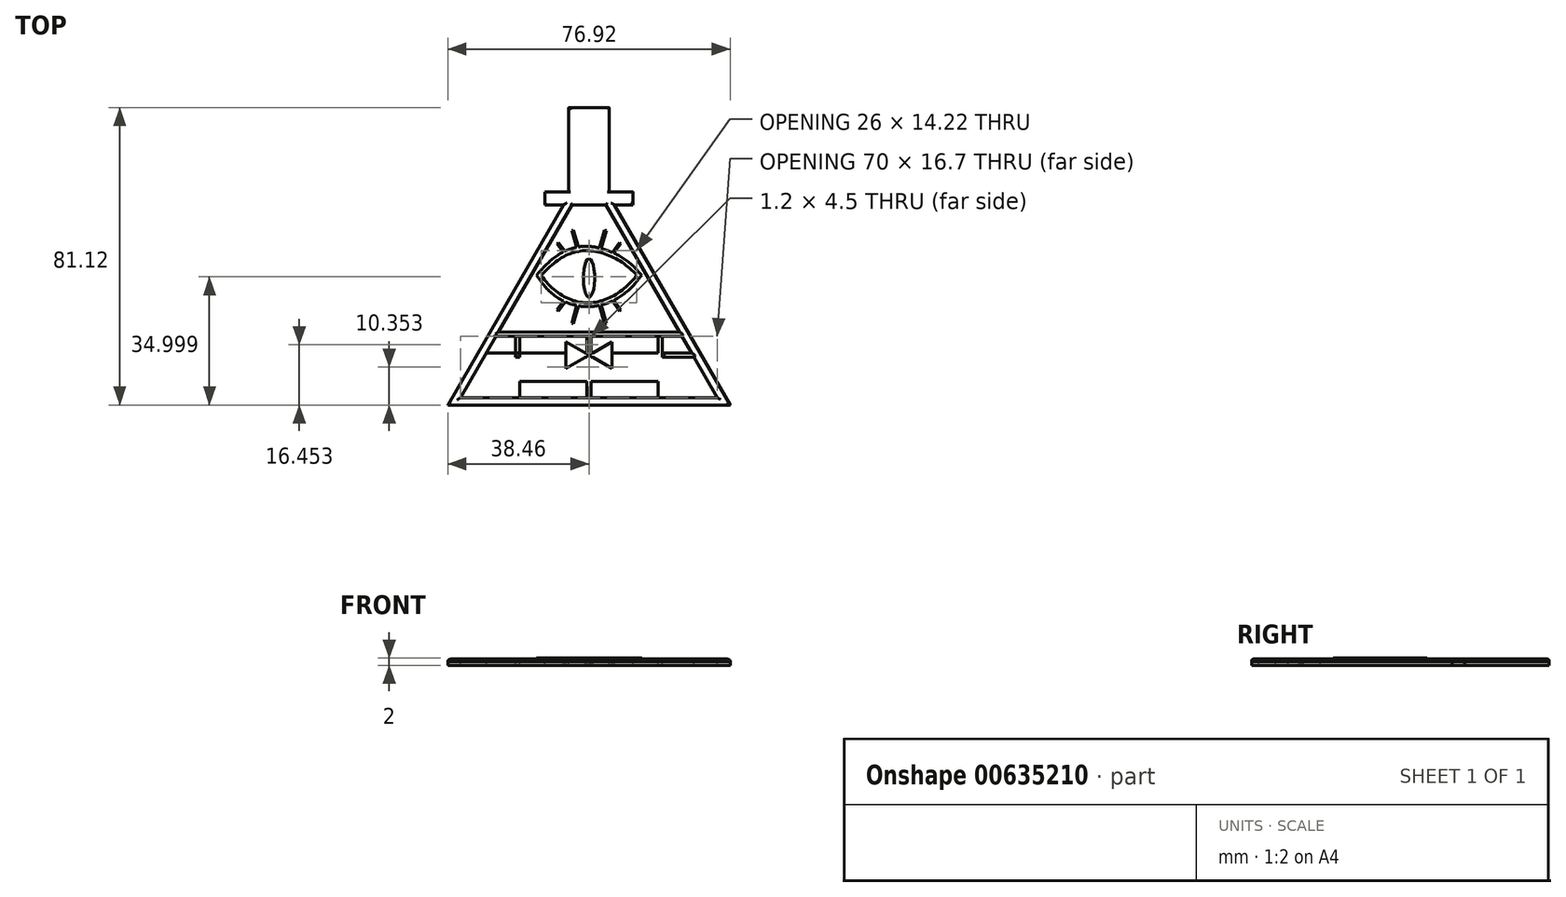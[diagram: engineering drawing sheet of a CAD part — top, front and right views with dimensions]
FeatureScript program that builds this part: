
annotation { "Feature Type Name" : "Feature", "Feature Type Description" : "" }
export const myFeature = defineFeature(function(context is Context, id is Id, definition is map)
    precondition{}
    {
        {
            var Q0;
            Q0=qCreatedBy(makeId("Top.planeOp"),FACE);
            var sketch = newSketch(context, id + "F0", { "sketchPlane" : qUnion([Q0])});
            skCircle(sketch, "E0.cCircle", {"center": v(0, 0) * mm, "radius": 20.2 * mm, "construction": true});
            skLineSegment(sketch, "E0.0", {"start": v(35, -20.2) * mm, "end": v(-35, -20.2) * mm});
            skLineSegment(sketch, "E0.1", {"start": v(-35, -20.2) * mm, "end": v(0, 40.41) * mm});
            skLineSegment(sketch, "E0.2", {"start": v(0, 40.41) * mm, "end": v(35, -20.2) * mm});
            skPoint(sketch, "E0.0.midPoint", {"position": v(0, -20.2) * mm});
            skLineSegment(sketch, "E1", {"start": v(0, 32.41) * mm, "end": v(12, 32.41) * mm});
            skLineSegment(sketch, "E2", {"start": v(12, 32.41) * mm, "end": v(12, 35.91) * mm});
            skLineSegment(sketch, "E3", {"start": v(12, 35.91) * mm, "end": v(-12, 35.91) * mm});
            skLineSegment(sketch, "E4", {"start": v(-12, 35.91) * mm, "end": v(-12, 32.41) * mm});
            skLineSegment(sketch, "E5", {"start": v(-12, 32.41) * mm, "end": v(0, 32.41) * mm});
            skLineSegment(sketch, "E6", {"start": v(0, 40.41) * mm, "end": v(0, 35.91) * mm});
            skLineSegment(sketch, "E7", {"start": v(-12, 35.91) * mm, "end": v(-5.5, 35.91) * mm});
            skLineSegment(sketch, "E8", {"start": v(-5.5, 35.91) * mm, "end": v(-5.5, 58.91) * mm});
            skLineSegment(sketch, "E9", {"start": v(12, 35.91) * mm, "end": v(6, 35.91) * mm});
            skPoint(sketch, "E9.endSnap0", {"position": v(6, 32.41) * mm});
            skLineSegment(sketch, "E10", {"start": v(12, 35.91) * mm, "end": v(5.5, 35.91) * mm});
            skLineSegment(sketch, "E11", {"start": v(5.5, 35.91) * mm, "end": v(5.5, 58.91) * mm});
            skLineSegment(sketch, "E12", {"start": v(5.5, 58.91) * mm, "end": v(-5.5, 58.91) * mm});
            skPoint(sketch, "E13", {"position": v(0, 12.4) * mm});
            skLineSegment(sketch, "E14", {"start": v(0, 5.68) * mm, "end": v(0, 19.9) * mm});
            skLineSegment(sketch, "E15", {"start": v(-13, 13.17) * mm, "end": v(13, 13.17) * mm});
            skFitSpline(sketch, "E16", {"points": [v(-13, 13.17) * mm, v(0, 19.9) * mm, v(13, 13.17) * mm], "startDerivative": vector(26.44, 29.26) * mm, "endDerivative": vector(19.77, -23.2) * mm});
            skFitSpline(sketch, "E17", {"points": [v(-13, 13.17) * mm, v(0, 5.68) * mm, v(13, 13.17) * mm], "startDerivative": vector(20.09, -29.42) * mm, "endDerivative": vector(20.07, 26.4) * mm});
            skLineSegment(sketch, "E18.0", {"start": v(38.46, -22.2) * mm, "end": v(-38.46, -22.2) * mm});
            skLineSegment(sketch, "E18.1", {"start": v(0, 44.41) * mm, "end": v(38.46, -22.2) * mm});
            skLineSegment(sketch, "E18.2", {"start": v(-38.46, -22.2) * mm, "end": v(0, 44.41) * mm});
            skEllipse(sketch, "E19", {"center": v(0, 12.4) * mm, "majorRadius": 5.25 * mm, "minorRadius": 1.53 * mm, "majorAxis": v(0, 1)});
            skFitSpline(sketch, "E20.0", {"points": [v(-13.74, 13.84) * mm, v(-12.61, 15.1) * mm, v(-10.4, 17.25) * mm, v(-7.04, 19.51) * mm, v(-3.58, 20.78) * mm, v(0.03, 21.05) * mm, v(3.79, 20.38) * mm, v(7.48, 18.9) * mm, v(10.92, 16.7) * mm, v(12.9, 14.84) * mm, v(13.76, 13.82) * mm]});
            skFitSpline(sketch, "E21.0", {"points": [v(-13.83, 12.6) * mm, v(-12.95, 11.33) * mm, v(-11, 9.04) * mm, v(-7.6, 6.5) * mm, v(-4.5, 5.22) * mm, v(-1.93, 4.73) * mm, v(0.03, 4.63) * mm, v(1.98, 4.83) * mm, v(4.54, 5.44) * mm, v(7.62, 6.82) * mm, v(10.98, 9.3) * mm, v(12.92, 11.42) * mm, v(13.8, 12.57) * mm]});
            skLineSegment(sketch, "E22", {"start": v(-11.84, 10.11) * mm, "end": v(-14.33, 13.23) * mm});
            skLineSegment(sketch, "E23", {"start": v(-13.6, 14) * mm, "end": v(-14.33, 13.23) * mm});
            skLineSegment(sketch, "E24.MirrorCS", {"start": v(13.6, 14) * mm, "end": v(14.33, 13.23) * mm});
            skLineSegment(sketch, "E25", {"start": v(13.11, 11.7) * mm, "end": v(14.33, 13.23) * mm});
            skLineSegment(sketch, "E26", {"start": v(-6.93, 19.4) * mm, "end": v(-8.7, 21.82) * mm});
            skLineSegment(sketch, "E27", {"start": v(-8.7, 21.82) * mm, "end": v(-8.29, 22.12) * mm});
            skLineSegment(sketch, "E28", {"start": v(-8.29, 22.12) * mm, "end": v(-6.48, 19.62) * mm});
            skLineSegment(sketch, "E29.MirrorCS", {"start": v(8.29, 22.12) * mm, "end": v(6.48, 19.62) * mm});
            skLineSegment(sketch, "E30.MirrorCS", {"start": v(6.93, 19.4) * mm, "end": v(8.7, 21.82) * mm});
            skLineSegment(sketch, "E31.MirrorCS", {"start": v(8.7, 21.82) * mm, "end": v(8.29, 22.12) * mm});
            skLineSegment(sketch, "E32", {"start": v(6.48, 19.62) * mm, "end": v(6.28, 19.33) * mm});
            skLineSegment(sketch, "E33", {"start": v(6.93, 19.4) * mm, "end": v(6.74, 19.12) * mm});
            skLineSegment(sketch, "E34", {"start": v(-2.88, 20.75) * mm, "end": v(-4.23, 25.56) * mm});
            skLineSegment(sketch, "E35", {"start": v(-4.23, 25.56) * mm, "end": v(-4.7, 25.43) * mm});
            skLineSegment(sketch, "E36", {"start": v(-4.7, 25.43) * mm, "end": v(-3.38, 20.65) * mm});
            skLineSegment(sketch, "E37.MirrorCS", {"start": v(2.88, 20.75) * mm, "end": v(4.23, 25.56) * mm});
            skLineSegment(sketch, "E38.MirrorCS", {"start": v(4.7, 25.43) * mm, "end": v(3.38, 20.65) * mm});
            skLineSegment(sketch, "E39.MirrorCS", {"start": v(4.23, 25.56) * mm, "end": v(4.7, 25.43) * mm});
            skLineSegment(sketch, "E40", {"start": v(3.38, 20.65) * mm, "end": v(3.3, 20.38) * mm});
            skLineSegment(sketch, "E41", {"start": v(2.88, 20.75) * mm, "end": v(2.81, 20.5) * mm});
            skLineSegment(sketch, "E42", {"start": v(0, 12.79) * mm, "end": v(-0.93, 12.79) * mm});
            skLineSegment(sketch, "E43.MirrorCS", {"start": v(-2.88, 4.83) * mm, "end": v(-4.23, 0.02) * mm});
            skLineSegment(sketch, "E44.MirrorCS", {"start": v(-4.7, 0.15) * mm, "end": v(-3.38, 4.92) * mm});
            skLineSegment(sketch, "E45.MirrorCS", {"start": v(-8.29, 3.46) * mm, "end": v(-6.48, 5.96) * mm});
            skLineSegment(sketch, "E46.MirrorCS", {"start": v(-6.93, 6.19) * mm, "end": v(-8.7, 3.76) * mm});
            skLineSegment(sketch, "E47.MirrorCS", {"start": v(-4.23, 0.02) * mm, "end": v(-4.7, 0.15) * mm});
            skLineSegment(sketch, "E48.MirrorCS", {"start": v(-8.7, 3.76) * mm, "end": v(-8.29, 3.46) * mm});
            skLineSegment(sketch, "E49.MirrorCS", {"start": v(4.23, 0.02) * mm, "end": v(4.7, 0.15) * mm});
            skLineSegment(sketch, "E50.MirrorCS", {"start": v(2.88, 4.83) * mm, "end": v(4.23, 0.02) * mm});
            skLineSegment(sketch, "E51.MirrorCS", {"start": v(4.7, 0.15) * mm, "end": v(3.38, 4.92) * mm});
            skLineSegment(sketch, "E52.MirrorCS", {"start": v(8.7, 3.76) * mm, "end": v(8.29, 3.46) * mm});
            skLineSegment(sketch, "E53.MirrorCS", {"start": v(8.29, 3.46) * mm, "end": v(6.48, 5.96) * mm});
            skLineSegment(sketch, "E54.MirrorCS", {"start": v(6.93, 6.19) * mm, "end": v(8.7, 3.76) * mm});
            skLineSegment(sketch, "E55", {"start": v(-6.93, 6.19) * mm, "end": v(-6.86, 6.3) * mm});
            skLineSegment(sketch, "E56", {"start": v(-6.48, 5.96) * mm, "end": v(-6.4, 6.07) * mm});
            skLineSegment(sketch, "E57", {"start": v(-3.38, 4.92) * mm, "end": v(-3.35, 5.02) * mm});
            skLineSegment(sketch, "E58", {"start": v(-2.88, 4.83) * mm, "end": v(-2.86, 4.92) * mm});
            skLineSegment(sketch, "E59", {"start": v(2.88, 4.83) * mm, "end": v(2.82, 5.04) * mm});
            skLineSegment(sketch, "E60", {"start": v(3.38, 4.92) * mm, "end": v(3.3, 5.16) * mm});
            skLineSegment(sketch, "E61", {"start": v(6.48, 5.96) * mm, "end": v(6.26, 6.27) * mm});
            skLineSegment(sketch, "E62", {"start": v(6.93, 6.19) * mm, "end": v(6.71, 6.5) * mm});
            skLineSegment(sketch, "E63", {"start": v(-25.36, -3.5) * mm, "end": v(25.36, -3.5) * mm});
            skLineSegment(sketch, "E64", {"start": v(0, -3.5) * mm, "end": v(0, -9.2) * mm, "construction": true});
            skLineSegment(sketch, "E65", {"start": v(0, -9.2) * mm, "end": v(28.65, -9.2) * mm});
            skLineSegment(sketch, "E66", {"start": v(0, -15.7) * mm, "end": v(32.4, -15.7) * mm});
            skLineSegment(sketch, "E67", {"start": v(0, -15.7) * mm, "end": v(0, -20.2) * mm, "construction": true});
            skLineSegment(sketch, "E68", {"start": v(0, -9.2) * mm, "end": v(-28.65, -9.2) * mm});
            skLineSegment(sketch, "E69", {"start": v(0, -15.7) * mm, "end": v(-32.4, -15.7) * mm});
            skLineSegment(sketch, "E70", {"start": v(-19.43, -15.7) * mm, "end": v(-19.43, -20.2) * mm, "construction": true});
            skLineSegment(sketch, "E71", {"start": v(-32.4, -15.7) * mm, "end": v(-19.43, -15.7) * mm});
            skLineSegment(sketch, "E72", {"start": v(-19.43, -15.7) * mm, "end": v(0, -15.7) * mm});
            skLineSegment(sketch, "E73", {"start": v(-9.72, -15.7) * mm, "end": v(-9.72, -9.2) * mm, "construction": true});
            skLineSegment(sketch, "E74", {"start": v(-19.43, -9.2) * mm, "end": v(-19.43, -3.5) * mm, "construction": true});
            skLineSegment(sketch, "E75", {"start": v(32.4, -15.7) * mm, "end": v(19.43, -15.7) * mm});
            skLineSegment(sketch, "E76", {"start": v(19.43, -15.7) * mm, "end": v(19.43, -20.2) * mm, "construction": true});
            skLineSegment(sketch, "E77", {"start": v(19.43, -15.7) * mm, "end": v(0, -15.7) * mm});
            skLineSegment(sketch, "E78", {"start": v(9.72, -15.7) * mm, "end": v(9.72, -9.2) * mm, "construction": true});
            skLineSegment(sketch, "E79", {"start": v(19.43, -9.2) * mm, "end": v(19.43, -3.5) * mm, "construction": true});
            skLineSegment(sketch, "E80", {"start": v(-31.25, -13.7) * mm, "end": v(31.25, -13.7) * mm});
            skLineSegment(sketch, "E81", {"start": v(-27.96, -8) * mm, "end": v(27.96, -8) * mm});
            skLineSegment(sketch, "E82", {"start": v(-24.67, -2.3) * mm, "end": v(24.67, -2.3) * mm});
            skLineSegment(sketch, "E83.bottom", {"start": v(-18.83, -15.7) * mm, "end": v(-20.03, -15.7) * mm});
            skLineSegment(sketch, "E83.top", {"start": v(-18.83, -20.2) * mm, "end": v(-20.03, -20.2) * mm});
            skLineSegment(sketch, "E83.left", {"start": v(-18.83, -15.7) * mm, "end": v(-18.83, -20.2) * mm});
            skLineSegment(sketch, "E83.right", {"start": v(-20.03, -15.7) * mm, "end": v(-20.03, -20.2) * mm});
            skPoint(sketch, "E83.middle", {"position": v(-19.43, -17.96) * mm});
            skLineSegment(sketch, "E84.bottom", {"start": v(0.6, -15.7) * mm, "end": v(-0.6, -15.7) * mm});
            skLineSegment(sketch, "E84.top", {"start": v(0.6, -20.2) * mm, "end": v(-0.6, -20.2) * mm});
            skLineSegment(sketch, "E84.left", {"start": v(0.6, -15.7) * mm, "end": v(0.6, -20.2) * mm});
            skLineSegment(sketch, "E84.right", {"start": v(-0.6, -15.7) * mm, "end": v(-0.6, -20.2) * mm});
            skPoint(sketch, "E84.middle", {"position": v(0, -17.96) * mm});
            skLineSegment(sketch, "E85.bottom", {"start": v(20.03, -15.7) * mm, "end": v(18.83, -15.7) * mm});
            skLineSegment(sketch, "E85.top", {"start": v(20.03, -20.2) * mm, "end": v(18.83, -20.2) * mm});
            skLineSegment(sketch, "E85.left", {"start": v(20.03, -15.7) * mm, "end": v(20.03, -20.2) * mm});
            skLineSegment(sketch, "E85.right", {"start": v(18.83, -15.7) * mm, "end": v(18.83, -20.2) * mm});
            skPoint(sketch, "E85.middle", {"position": v(19.43, -17.96) * mm});
            skLineSegment(sketch, "E86.bottom", {"start": v(-9.12, -15.7) * mm, "end": v(-10.32, -15.7) * mm});
            skLineSegment(sketch, "E86.top", {"start": v(-9.12, -9.2) * mm, "end": v(-10.32, -9.2) * mm});
            skLineSegment(sketch, "E86.left", {"start": v(-9.12, -15.7) * mm, "end": v(-9.12, -9.2) * mm});
            skLineSegment(sketch, "E86.right", {"start": v(-10.32, -15.7) * mm, "end": v(-10.32, -9.2) * mm});
            skPoint(sketch, "E86.middle", {"position": v(-9.72, -12.46) * mm});
            skLineSegment(sketch, "E87.bottom", {"start": v(10.32, -15.7) * mm, "end": v(9.12, -15.7) * mm});
            skLineSegment(sketch, "E87.top", {"start": v(10.32, -9.2) * mm, "end": v(9.12, -9.2) * mm});
            skLineSegment(sketch, "E87.left", {"start": v(10.32, -15.7) * mm, "end": v(10.32, -9.2) * mm});
            skLineSegment(sketch, "E87.right", {"start": v(9.12, -15.7) * mm, "end": v(9.12, -9.2) * mm});
            skPoint(sketch, "E87.middle", {"position": v(9.72, -12.46) * mm});
            skLineSegment(sketch, "E88.bottom", {"start": v(0.6, -9.2) * mm, "end": v(-0.6, -9.2) * mm});
            skLineSegment(sketch, "E88.top", {"start": v(0.6, -3.5) * mm, "end": v(-0.6, -3.5) * mm});
            skLineSegment(sketch, "E88.left", {"start": v(0.6, -9.2) * mm, "end": v(0.6, -3.5) * mm});
            skLineSegment(sketch, "E88.right", {"start": v(-0.6, -9.2) * mm, "end": v(-0.6, -3.5) * mm});
            skPoint(sketch, "E88.middle", {"position": v(0, -6.36) * mm});
            skLineSegment(sketch, "E89.bottom", {"start": v(20.03, -9.2) * mm, "end": v(18.83, -9.2) * mm});
            skLineSegment(sketch, "E89.top", {"start": v(20.03, -3.5) * mm, "end": v(18.83, -3.5) * mm});
            skLineSegment(sketch, "E89.left", {"start": v(20.03, -9.2) * mm, "end": v(20.03, -3.5) * mm});
            skLineSegment(sketch, "E89.right", {"start": v(18.83, -9.2) * mm, "end": v(18.83, -3.5) * mm});
            skPoint(sketch, "E89.middle", {"position": v(19.43, -6.36) * mm});
            skLineSegment(sketch, "E90", {"start": v(-19.43, -9.2) * mm, "end": v(-20.43, -9.2) * mm});
            skLineSegment(sketch, "E91.bottom", {"start": v(-18.83, -9.2) * mm, "end": v(-20.03, -9.2) * mm});
            skLineSegment(sketch, "E91.top", {"start": v(-18.83, -3.5) * mm, "end": v(-20.03, -3.5) * mm});
            skLineSegment(sketch, "E91.left", {"start": v(-18.83, -9.2) * mm, "end": v(-18.83, -3.5) * mm});
            skLineSegment(sketch, "E91.right", {"start": v(-20.03, -9.2) * mm, "end": v(-20.03, -3.5) * mm});
            skPoint(sketch, "E91.middle", {"position": v(-19.43, -6.36) * mm});
            skCircle(sketch, "E92.cCircle", {"center": v(4.2, -8.6) * mm, "radius": 4.2 * mm, "construction": true});
            skLineSegment(sketch, "E92.0", {"start": v(0, -8.6) * mm, "end": v(6.3, -4.97) * mm});
            skLineSegment(sketch, "E92.1", {"start": v(6.3, -4.97) * mm, "end": v(6.3, -12.24) * mm});
            skLineSegment(sketch, "E92.2", {"start": v(6.3, -12.24) * mm, "end": v(0, -8.6) * mm});
            skLineSegment(sketch, "E93.MirrorCS", {"start": v(0, -8.6) * mm, "end": v(-6.3, -4.97) * mm});
            skLineSegment(sketch, "E94.MirrorCS", {"start": v(-6.3, -12.24) * mm, "end": v(0, -8.6) * mm});
            skLineSegment(sketch, "E95.MirrorCS", {"start": v(-6.3, -4.97) * mm, "end": v(-6.3, -12.24) * mm});
            skSolve(sketch);
        }
        {
            var Q0;
            {var subQ1=sQuery(id+"F0.wireOp",EDGE,"E4");Q0=makeQuery(id+"F0.imprint","IMPRINT",FACE,{"disambiguationData":[TD([[makeQuery(id+"F0.imprint","IMPRINT",EDGE,{"derivedFrom":subQ1}),1.0]])]});}
            var Q1;
            {var subQ5=sQuery(id+"F0.wireOp",EDGE,"E2");Q1=makeQuery(id+"F0.imprint","IMPRINT",FACE,{"disambiguationData":[TD([[makeQuery(id+"F0.imprint","IMPRINT",EDGE,{"derivedFrom":subQ5}),1.0]])]});}
            var Q2;
            {var subQ0=sQuery(id+"F0.wireOp",EDGE,"E3");var subQ1=sQuery(id+"F0.wireOp",EDGE,"E0.2");var subQ2=makeQuery(id+"F0.imprint","INTERSECT",VERTEX,{"derivedFrom":[subQ1,subQ0]});Q2=makeQuery(id+"F0.imprint","IMPRINT",FACE,{"disambiguationData":[TD([[makeQuery(id+"F0.imprint","IMPRINT",EDGE,{"disambiguationData":[TD([[subQ2,-1.0]])],"derivedFrom":subQ1}),1.0]])]});}
            var Q3;
            {var subQ0=sQuery(id+"F0.wireOp",EDGE,"E5");var subQ1=sQuery(id+"F0.wireOp",EDGE,"E0.1");var subQ2=makeQuery(id+"F0.imprint","INTERSECT",VERTEX,{"derivedFrom":[subQ1,subQ0]});Q3=makeQuery(id+"F0.imprint","IMPRINT",FACE,{"disambiguationData":[TD([[makeQuery(id+"F0.imprint","IMPRINT",EDGE,{"disambiguationData":[TD([[subQ2,-1.0]])],"derivedFrom":subQ1}),1.0]])]});}
            var Q4;
            {var subQ4=sQuery(id+"F0.wireOp",EDGE,"E5");var subQ8=sQuery(id+"F0.wireOp",EDGE,"E0.1");var subQ9=makeQuery(id+"F0.imprint","INTERSECT",VERTEX,{"derivedFrom":[subQ8,subQ4]});Q4=makeQuery(id+"F0.imprint","IMPRINT",FACE,{"disambiguationData":[TD([[makeQuery(id+"F0.imprint","IMPRINT",EDGE,{"disambiguationData":[TD([[subQ9,-1.0]])],"derivedFrom":subQ8}),-1.0]])]});}
            var Q5;
            {var subQ0=sQuery(id+"F0.wireOp",EDGE,"E6");Q5=makeQuery(id+"F0.imprint","IMPRINT",FACE,{"disambiguationData":[TD([[makeQuery(id+"F0.imprint","IMPRINT",EDGE,{"derivedFrom":subQ0}),-1.0]])]});}
            var Q6;
            {var subQ0=sQuery(id+"F0.wireOp",EDGE,"E6");Q6=makeQuery(id+"F0.imprint","IMPRINT",FACE,{"disambiguationData":[TD([[makeQuery(id+"F0.imprint","IMPRINT",EDGE,{"derivedFrom":subQ0}),1.0]])]});}
            var Q7;
            {var subQ0=sQuery(id+"F0.wireOp",EDGE,"E3");var subQ5=sQuery(id+"F0.wireOp",EDGE,"E0.2");var subQ7=makeQuery(id+"F0.imprint","INTERSECT",VERTEX,{"derivedFrom":[subQ5,subQ0]});Q7=makeQuery(id+"F0.imprint","IMPRINT",FACE,{"disambiguationData":[TD([[makeQuery(id+"F0.imprint","IMPRINT",EDGE,{"disambiguationData":[TD([[subQ7,1.0]])],"derivedFrom":subQ0}),-1.0]])]});}
            var Q8;
            {var subQ1=sQuery(id+"F0.wireOp",EDGE,"E8");Q8=makeQuery(id+"F0.imprint","IMPRINT",FACE,{"disambiguationData":[TD([[makeQuery(id+"F0.imprint","IMPRINT",EDGE,{"derivedFrom":subQ1}),-1.0]])]});}
            extrude(context, id + "F1", {"entities" : qUnion([Q0, Q1, Q2, Q3, Q4, Q5, Q6, Q7, Q8]), "depth" : 0.7 * mm, "offsetDistance" : 25 * mm});
        }
        {
            var Q0;
            {var subQ1=sQuery(id+"F0.wireOp",EDGE,"E18.0");Q0=makeQuery(id+"F0.imprint","IMPRINT",FACE,{"disambiguationData":[TD([[makeQuery(id+"F0.imprint","IMPRINT",EDGE,{"derivedFrom":subQ1}),-1.0]])]});}
            var Q1;
            {var subQ5=sQuery(id+"F0.wireOp",EDGE,"E82");Q1=makeQuery(id+"F0.imprint","IMPRINT",FACE,{"disambiguationData":[TD([[makeQuery(id+"F0.imprint","IMPRINT",EDGE,{"derivedFrom":subQ5}),-1.0]])]});}
            var Q2;
            {var subQ5=sQuery(id+"F0.wireOp",EDGE,"E86.top");Q2=makeQuery(id+"F0.imprint","IMPRINT",FACE,{"disambiguationData":[TD([[makeQuery(id+"F0.imprint","IMPRINT",EDGE,{"derivedFrom":subQ5}),-1.0]])]});}
            var Q3;
            {var subQ0=sQuery(id+"F0.wireOp",EDGE,"E90");Q3=makeQuery(id+"F0.imprint","IMPRINT",FACE,{"disambiguationData":[TD([[makeQuery(id+"F0.imprint","IMPRINT",EDGE,{"derivedFrom":subQ0}),-1.0]])]});}
            var Q4;
            {var subQ3=sQuery(id+"F0.wireOp",EDGE,"E81");var subQ6=sQuery(id+"F0.wireOp",EDGE,"E91.right");var subQ7=makeQuery(id+"F0.imprint","INTERSECT",VERTEX,{"derivedFrom":[subQ3,subQ6]});Q4=makeQuery(id+"F0.imprint","IMPRINT",FACE,{"disambiguationData":[TD([[makeQuery(id+"F0.imprint","IMPRINT",EDGE,{"disambiguationData":[TD([[subQ7,-1.0]])],"derivedFrom":subQ3}),-1.0]])]});}
            var Q5;
            {var subQ0=sQuery(id+"F0.wireOp",EDGE,"E87.top");Q5=makeQuery(id+"F0.imprint","IMPRINT",FACE,{"disambiguationData":[TD([[makeQuery(id+"F0.imprint","IMPRINT",EDGE,{"derivedFrom":subQ0}),-1.0]])]});}
            var Q6;
            {var subQ5=sQuery(id+"F0.wireOp",EDGE,"E88.bottom");Q6=makeQuery(id+"F0.imprint","IMPRINT",FACE,{"disambiguationData":[TD([[makeQuery(id+"F0.imprint","IMPRINT",EDGE,{"derivedFrom":subQ5}),-1.0]])]});}
            var Q7;
            {var subQ0=sQuery(id+"F0.wireOp",EDGE,"E65");var subQ1=sQuery(id+"F0.wireOp",EDGE,"E0.2");var subQ2=makeQuery(id+"F0.imprint","INTERSECT",VERTEX,{"derivedFrom":[subQ1,subQ0]});Q7=makeQuery(id+"F0.imprint","IMPRINT",FACE,{"disambiguationData":[TD([[makeQuery(id+"F0.imprint","IMPRINT",EDGE,{"disambiguationData":[TD([[subQ2,1.0]])],"derivedFrom":subQ1}),-1.0]])]});}
            var Q8;
            {var subQ5=sQuery(id+"F0.wireOp",EDGE,"E89.bottom");Q8=makeQuery(id+"F0.imprint","IMPRINT",FACE,{"disambiguationData":[TD([[makeQuery(id+"F0.imprint","IMPRINT",EDGE,{"derivedFrom":subQ5}),-1.0]])]});}
            var Q9;
            {var subQ5=sQuery(id+"F0.wireOp",EDGE,"E89.top");Q9=makeQuery(id+"F0.imprint","IMPRINT",FACE,{"disambiguationData":[TD([[makeQuery(id+"F0.imprint","IMPRINT",EDGE,{"derivedFrom":subQ5}),1.0]])]});}
            var Q10;
            {var subQ5=sQuery(id+"F0.wireOp",EDGE,"E88.top");Q10=makeQuery(id+"F0.imprint","IMPRINT",FACE,{"disambiguationData":[TD([[makeQuery(id+"F0.imprint","IMPRINT",EDGE,{"derivedFrom":subQ5}),1.0]])]});}
            var Q11;
            {var subQ5=sQuery(id+"F0.wireOp",EDGE,"E91.top");Q11=makeQuery(id+"F0.imprint","IMPRINT",FACE,{"disambiguationData":[TD([[makeQuery(id+"F0.imprint","IMPRINT",EDGE,{"derivedFrom":subQ5}),1.0]])]});}
            var Q12;
            {var subQ0=sQuery(id+"F0.wireOp",EDGE,"E71");Q12=makeQuery(id+"F0.imprint","IMPRINT",FACE,{"disambiguationData":[TD([[makeQuery(id+"F0.imprint","IMPRINT",EDGE,{"derivedFrom":subQ0}),1.0]])]});}
            var Q13;
            Q13=makeQuery(id+"F0.imprint","IMPRINT",FACE,{"disambiguationData":[TD([[makeQuery(id+"F0.imprint","IMPRINT",EDGE,{"derivedFrom":sQuery(id+"F0.wireOp",EDGE,"E83.bottom")}),1.0]])]});
            var Q14;
            {var subQ5=sQuery(id+"F0.wireOp",EDGE,"E86.top");Q14=makeQuery(id+"F0.imprint","IMPRINT",FACE,{"disambiguationData":[TD([[makeQuery(id+"F0.imprint","IMPRINT",EDGE,{"derivedFrom":subQ5}),1.0]])]});}
            var Q15;
            {var subQ5=sQuery(id+"F0.wireOp",EDGE,"E86.bottom");Q15=makeQuery(id+"F0.imprint","IMPRINT",FACE,{"disambiguationData":[TD([[makeQuery(id+"F0.imprint","IMPRINT",EDGE,{"derivedFrom":subQ5}),-1.0]])]});}
            var Q16;
            {var subQ0=sQuery(id+"F0.wireOp",EDGE,"E84.bottom");Q16=makeQuery(id+"F0.imprint","IMPRINT",FACE,{"disambiguationData":[TD([[makeQuery(id+"F0.imprint","IMPRINT",EDGE,{"derivedFrom":subQ0}),-1.0]])]});}
            var Q17;
            {var subQ5=sQuery(id+"F0.wireOp",EDGE,"E87.top");Q17=makeQuery(id+"F0.imprint","IMPRINT",FACE,{"disambiguationData":[TD([[makeQuery(id+"F0.imprint","IMPRINT",EDGE,{"derivedFrom":subQ5}),1.0]])]});}
            var Q18;
            {var subQ5=sQuery(id+"F0.wireOp",EDGE,"E87.bottom");Q18=makeQuery(id+"F0.imprint","IMPRINT",FACE,{"disambiguationData":[TD([[makeQuery(id+"F0.imprint","IMPRINT",EDGE,{"derivedFrom":subQ5}),-1.0]])]});}
            var Q19;
            {var subQ8=sQuery(id+"F0.wireOp",EDGE,"E75");Q19=makeQuery(id+"F0.imprint","IMPRINT",FACE,{"disambiguationData":[TD([[makeQuery(id+"F0.imprint","IMPRINT",EDGE,{"derivedFrom":subQ8}),-1.0]])]});}
            var Q20;
            Q20=makeQuery(id+"F0.imprint","IMPRINT",FACE,{"disambiguationData":[TD([[makeQuery(id+"F0.imprint","IMPRINT",EDGE,{"derivedFrom":sQuery(id+"F0.wireOp",EDGE,"E85.bottom")}),1.0]])]});
            var Q21;
            Q21=makeQuery(id+"F0.imprint","IMPRINT",FACE,{"disambiguationData":[TD([[makeQuery(id+"F0.imprint","IMPRINT",EDGE,{"derivedFrom":sQuery(id+"F0.wireOp",EDGE,"E84.bottom")}),1.0]])]});
            var Q22;
            {var subQ1=sQuery(id+"F0.wireOp",EDGE,"E81");var subQ5=sQuery(id+"F0.wireOp",EDGE,"E95.MirrorCS");var subQ6=makeQuery(id+"F0.imprint","INTERSECT",VERTEX,{"derivedFrom":[subQ1,subQ5]});Q22=makeQuery(id+"F0.imprint","IMPRINT",FACE,{"disambiguationData":[TD([[makeQuery(id+"F0.imprint","IMPRINT",EDGE,{"disambiguationData":[TD([[subQ6,-1.0]])],"derivedFrom":subQ1}),-1.0]])]});}
            var Q23;
            {var subQ3=sQuery(id+"F0.wireOp",EDGE,"E95.MirrorCS");var subQ5=sQuery(id+"F0.wireOp",EDGE,"E94.MirrorCS");var subQ6=makeQuery(id+"F0.imprint","INTERSECT",VERTEX,{"derivedFrom":[subQ5,subQ3]});Q23=makeQuery(id+"F0.imprint","IMPRINT",FACE,{"disambiguationData":[TD([[makeQuery(id+"F0.imprint","IMPRINT",EDGE,{"disambiguationData":[TD([[subQ6,-1.0]])],"derivedFrom":subQ5}),1.0]])]});}
            var Q24;
            {var subQ3=sQuery(id+"F0.wireOp",EDGE,"E92.1");var subQ5=sQuery(id+"F0.wireOp",EDGE,"E92.2");var subQ7=makeQuery(id+"F0.imprint","INTERSECT",VERTEX,{"derivedFrom":[subQ3,subQ5]});Q24=makeQuery(id+"F0.imprint","IMPRINT",FACE,{"disambiguationData":[TD([[makeQuery(id+"F0.imprint","IMPRINT",EDGE,{"disambiguationData":[TD([[subQ7,1.0]])],"derivedFrom":subQ3}),-1.0]])]});}
            var Q25;
            {var subQ3=sQuery(id+"F0.wireOp",EDGE,"E92.0");var subQ5=sQuery(id+"F0.wireOp",EDGE,"E81");var subQ6=makeQuery(id+"F0.imprint","INTERSECT",VERTEX,{"derivedFrom":[subQ5,subQ3]});Q25=makeQuery(id+"F0.imprint","IMPRINT",FACE,{"disambiguationData":[TD([[makeQuery(id+"F0.imprint","IMPRINT",EDGE,{"disambiguationData":[TD([[subQ6,-1.0]])],"derivedFrom":subQ5}),-1.0]])]});}
            var Q26;
            {var subQ0=sQuery(id+"F0.wireOp",EDGE,"E92.0");var subQ1=sQuery(id+"F0.wireOp",EDGE,"E81");var subQ2=makeQuery(id+"F0.imprint","INTERSECT",VERTEX,{"derivedFrom":[subQ1,subQ0]});Q26=makeQuery(id+"F0.imprint","IMPRINT",FACE,{"disambiguationData":[TD([[makeQuery(id+"F0.imprint","IMPRINT",EDGE,{"disambiguationData":[TD([[subQ2,-1.0]])],"derivedFrom":subQ1}),1.0]])]});}
            var Q27;
            {var subQ0=sQuery(id+"F0.wireOp",EDGE,"E95.MirrorCS");var subQ1=sQuery(id+"F0.wireOp",EDGE,"E81");var subQ2=makeQuery(id+"F0.imprint","INTERSECT",VERTEX,{"derivedFrom":[subQ1,subQ0]});Q27=makeQuery(id+"F0.imprint","IMPRINT",FACE,{"disambiguationData":[TD([[makeQuery(id+"F0.imprint","IMPRINT",EDGE,{"disambiguationData":[TD([[subQ2,-1.0]])],"derivedFrom":subQ1}),1.0]])]});}
            var Q28;
            {var subQ0=sQuery(id+"F0.wireOp",EDGE,"E93.MirrorCS");var subQ1=sQuery(id+"F0.wireOp",EDGE,"E81");var subQ2=makeQuery(id+"F0.imprint","INTERSECT",VERTEX,{"derivedFrom":[subQ1,subQ0]});Q28=makeQuery(id+"F0.imprint","IMPRINT",FACE,{"disambiguationData":[TD([[makeQuery(id+"F0.imprint","IMPRINT",EDGE,{"disambiguationData":[TD([[subQ2,-1.0]])],"derivedFrom":subQ1}),-1.0]])]});}
            var Q29;
            {var subQ0=sQuery(id+"F0.wireOp",EDGE,"E88.right");var subQ1=sQuery(id+"F0.wireOp",EDGE,"E81");var subQ2=makeQuery(id+"F0.imprint","INTERSECT",VERTEX,{"derivedFrom":[subQ1,subQ0]});Q29=makeQuery(id+"F0.imprint","IMPRINT",FACE,{"disambiguationData":[TD([[makeQuery(id+"F0.imprint","IMPRINT",EDGE,{"disambiguationData":[TD([[subQ2,-1.0]])],"derivedFrom":subQ1}),-1.0]])]});}
            var Q30;
            {var subQ0=sQuery(id+"F0.wireOp",EDGE,"E88.left");var subQ1=sQuery(id+"F0.wireOp",EDGE,"E81");var subQ2=makeQuery(id+"F0.imprint","INTERSECT",VERTEX,{"derivedFrom":[subQ1,subQ0]});Q30=makeQuery(id+"F0.imprint","IMPRINT",FACE,{"disambiguationData":[TD([[makeQuery(id+"F0.imprint","IMPRINT",EDGE,{"disambiguationData":[TD([[subQ2,-1.0]])],"derivedFrom":subQ1}),-1.0]])]});}
            var Q31;
            {var subQ1=sQuery(id+"F0.wireOp",EDGE,"E88.bottom");var subQ3=sQuery(id+"F0.wireOp",EDGE,"E92.2");var subQ4=makeQuery(id+"F0.imprint","INTERSECT",VERTEX,{"derivedFrom":[subQ1,subQ3]});Q31=makeQuery(id+"F0.imprint","IMPRINT",FACE,{"disambiguationData":[TD([[makeQuery(id+"F0.imprint","IMPRINT",EDGE,{"disambiguationData":[TD([[subQ4,1.0]])],"derivedFrom":subQ1}),-1.0]])]});}
            var Q32;
            {var subQ1=sQuery(id+"F0.wireOp",EDGE,"E88.bottom");var subQ3=sQuery(id+"F0.wireOp",EDGE,"E94.MirrorCS");var subQ4=makeQuery(id+"F0.imprint","INTERSECT",VERTEX,{"derivedFrom":[subQ1,subQ3]});Q32=makeQuery(id+"F0.imprint","IMPRINT",FACE,{"disambiguationData":[TD([[makeQuery(id+"F0.imprint","IMPRINT",EDGE,{"disambiguationData":[TD([[subQ4,-1.0]])],"derivedFrom":subQ1}),-1.0]])]});}
            var Q33;
            {var subQ0=sQuery(id+"F0.wireOp",EDGE,"E94.MirrorCS");var subQ1=sQuery(id+"F0.wireOp",EDGE,"E88.right");var subQ2=makeQuery(id+"F0.imprint","INTERSECT",VERTEX,{"derivedFrom":[subQ1,subQ0]});Q33=makeQuery(id+"F0.imprint","IMPRINT",FACE,{"disambiguationData":[TD([[makeQuery(id+"F0.imprint","IMPRINT",EDGE,{"disambiguationData":[TD([[subQ2,-1.0]])],"derivedFrom":subQ1}),-1.0]])]});}
            var Q34;
            {var subQ0=sQuery(id+"F0.wireOp",EDGE,"E92.2");var subQ1=sQuery(id+"F0.wireOp",EDGE,"E88.left");var subQ2=makeQuery(id+"F0.imprint","INTERSECT",VERTEX,{"derivedFrom":[subQ1,subQ0]});Q34=makeQuery(id+"F0.imprint","IMPRINT",FACE,{"disambiguationData":[TD([[makeQuery(id+"F0.imprint","IMPRINT",EDGE,{"disambiguationData":[TD([[subQ2,-1.0]])],"derivedFrom":subQ1}),1.0]])]});}
            var Q35;
            {var subQ1=sQuery(id+"F0.wireOp",EDGE,"E68");var subQ3=sQuery(id+"F0.wireOp",EDGE,"E94.MirrorCS");var subQ4=makeQuery(id+"F0.imprint","INTERSECT",VERTEX,{"derivedFrom":[subQ1,subQ3]});Q35=makeQuery(id+"F0.imprint","IMPRINT",FACE,{"disambiguationData":[TD([[makeQuery(id+"F0.imprint","IMPRINT",EDGE,{"disambiguationData":[TD([[subQ4,-1.0]])],"derivedFrom":subQ3}),-1.0]])]});}
            var Q36;
            {var subQ1=sQuery(id+"F0.wireOp",EDGE,"E65");var subQ3=sQuery(id+"F0.wireOp",EDGE,"E92.2");var subQ4=makeQuery(id+"F0.imprint","INTERSECT",VERTEX,{"derivedFrom":[subQ1,subQ3]});Q36=makeQuery(id+"F0.imprint","IMPRINT",FACE,{"disambiguationData":[TD([[makeQuery(id+"F0.imprint","IMPRINT",EDGE,{"disambiguationData":[TD([[subQ4,-1.0]])],"derivedFrom":subQ3}),1.0]])]});}
            extrude(context, id + "F2", {"entities" : qUnion([Q0, Q1, Q2, Q3, Q4, Q5, Q6, Q7, Q8, Q9, Q10, Q11, Q12, Q13, Q14, Q15, Q16, Q17, Q18, Q19, Q20, Q21, Q22, Q23, Q24, Q25, Q26, Q27, Q28, Q29, Q30, Q31, Q32, Q33, Q34, Q35, Q36]), "operationType" : NewBodyOperationType.ADD, "depth" : 0.7 * mm, "offsetDistance" : 25 * mm});
        }
        {
            var Q0;
            {var subQ21=sQuery(id+"F0.wireOp",EDGE,"E22");Q0=makeQuery(id+"F0.imprint","IMPRINT",FACE,{"disambiguationData":[TD([[makeQuery(id+"F0.imprint","IMPRINT",EDGE,{"derivedFrom":subQ21}),-1.0]])]});}
            var Q1;
            {var subQ0=sQuery(id+"F0.wireOp",EDGE,"E34");Q1=makeQuery(id+"F0.imprint","IMPRINT",FACE,{"disambiguationData":[TD([[makeQuery(id+"F0.imprint","IMPRINT",EDGE,{"derivedFrom":subQ0}),1.0]])]});}
            var Q2;
            {var subQ0=sQuery(id+"F0.wireOp",EDGE,"E26");Q2=makeQuery(id+"F0.imprint","IMPRINT",FACE,{"disambiguationData":[TD([[makeQuery(id+"F0.imprint","IMPRINT",EDGE,{"derivedFrom":subQ0}),-1.0]])]});}
            var Q3;
            Q3=makeQuery(id+"F0.imprint","IMPRINT",FACE,{"disambiguationData":[TD([[makeQuery(id+"F0.imprint","IMPRINT",EDGE,{"derivedFrom":sQuery(id+"F0.wireOp",EDGE,"E37.MirrorCS")}),-1.0]])]});
            var Q4;
            Q4=makeQuery(id+"F0.imprint","IMPRINT",FACE,{"disambiguationData":[TD([[makeQuery(id+"F0.imprint","IMPRINT",EDGE,{"derivedFrom":sQuery(id+"F0.wireOp",EDGE,"E29.MirrorCS")}),1.0]])]});
            var Q5;
            Q5=makeQuery(id+"F0.imprint","IMPRINT",FACE,{"disambiguationData":[TD([[makeQuery(id+"F0.imprint","IMPRINT",EDGE,{"derivedFrom":sQuery(id+"F0.wireOp",EDGE,"E52.MirrorCS")}),-1.0]])]});
            var Q6;
            Q6=makeQuery(id+"F0.imprint","IMPRINT",FACE,{"disambiguationData":[TD([[makeQuery(id+"F0.imprint","IMPRINT",EDGE,{"derivedFrom":sQuery(id+"F0.wireOp",EDGE,"E49.MirrorCS")}),1.0]])]});
            var Q7;
            Q7=makeQuery(id+"F0.imprint","IMPRINT",FACE,{"disambiguationData":[TD([[makeQuery(id+"F0.imprint","IMPRINT",EDGE,{"derivedFrom":sQuery(id+"F0.wireOp",EDGE,"E43.MirrorCS")}),-1.0]])]});
            var Q8;
            Q8=makeQuery(id+"F0.imprint","IMPRINT",FACE,{"disambiguationData":[TD([[makeQuery(id+"F0.imprint","IMPRINT",EDGE,{"derivedFrom":sQuery(id+"F0.wireOp",EDGE,"E45.MirrorCS")}),1.0]])]});
            var Q9;
            {var subQ0=sQuery(id+"F0.wireOp",EDGE,"E14");var subQ1=makeQuery(id+"F0.imprint","IMPRINT",VERTEX,{"derivedFrom":subQ0});Q9=makeQuery(id+"F0.imprint","IMPRINT",FACE,{"disambiguationData":[TD([[makeQuery(id+"F0.imprint","IMPRINT",EDGE,{"disambiguationData":[TD([[subQ1,1.0]])],"derivedFrom":subQ0}),-1.0]])]});}
            var Q10;
            {var subQ0=sQuery(id+"F0.wireOp",EDGE,"E14");var subQ1=makeQuery(id+"F0.imprint","IMPRINT",VERTEX,{"derivedFrom":subQ0});Q10=makeQuery(id+"F0.imprint","IMPRINT",FACE,{"disambiguationData":[TD([[makeQuery(id+"F0.imprint","IMPRINT",EDGE,{"disambiguationData":[TD([[subQ1,1.0]])],"derivedFrom":subQ0}),1.0]])]});}
            var Q11;
            {var subQ0=sQuery(id+"F0.wireOp",EDGE,"E15");var subQ1=sQuery(id+"F0.wireOp",EDGE,"E14");var subQ2=makeQuery(id+"F0.imprint","INTERSECT",VERTEX,{"derivedFrom":[subQ1,subQ0]});Q11=makeQuery(id+"F0.imprint","IMPRINT",FACE,{"disambiguationData":[TD([[makeQuery(id+"F0.imprint","IMPRINT",EDGE,{"disambiguationData":[TD([[subQ2,-1.0]])],"derivedFrom":subQ1}),1.0]])]});}
            var Q12;
            {var subQ0=sQuery(id+"F0.wireOp",EDGE,"E15");var subQ1=sQuery(id+"F0.wireOp",EDGE,"E14");var subQ2=makeQuery(id+"F0.imprint","INTERSECT",VERTEX,{"derivedFrom":[subQ1,subQ0]});Q12=makeQuery(id+"F0.imprint","IMPRINT",FACE,{"disambiguationData":[TD([[makeQuery(id+"F0.imprint","IMPRINT",EDGE,{"disambiguationData":[TD([[subQ2,-1.0]])],"derivedFrom":subQ1}),-1.0]])]});}
            extrude(context, id + "F3", {"entities" : qUnion([Q0, Q1, Q2, Q3, Q4, Q5, Q6, Q7, Q8, Q9, Q10, Q11, Q12]), "depth" : 1 * mm, "offsetDistance" : 25 * mm});
        }
        {
            var Q0;
            {var subQ5=sQuery(id+"F0.wireOp",EDGE,"E82");Q0=makeQuery(id+"F0.imprint","IMPRINT",FACE,{"disambiguationData":[TD([[makeQuery(id+"F0.imprint","IMPRINT",EDGE,{"derivedFrom":subQ5}),-1.0]])]});}
            var Q1;
            {var subQ0=sQuery(id+"F0.wireOp",EDGE,"E6");Q1=makeQuery(id+"F0.imprint","IMPRINT",FACE,{"disambiguationData":[TD([[makeQuery(id+"F0.imprint","IMPRINT",EDGE,{"derivedFrom":subQ0}),-1.0]])]});}
            var Q2;
            {var subQ0=sQuery(id+"F0.wireOp",EDGE,"E84.left");Q2=makeQuery(id+"F0.imprint","IMPRINT",FACE,{"disambiguationData":[TD([[makeQuery(id+"F0.imprint","IMPRINT",EDGE,{"derivedFrom":subQ0}),1.0]])]});}
            var Q3;
            {var subQ0=sQuery(id+"F0.wireOp",EDGE,"E6");Q3=makeQuery(id+"F0.imprint","IMPRINT",FACE,{"disambiguationData":[TD([[makeQuery(id+"F0.imprint","IMPRINT",EDGE,{"derivedFrom":subQ0}),1.0]])]});}
            var Q4;
            {var subQ0=sQuery(id+"F0.wireOp",EDGE,"E86.top");Q4=makeQuery(id+"F0.imprint","IMPRINT",FACE,{"disambiguationData":[TD([[makeQuery(id+"F0.imprint","IMPRINT",EDGE,{"derivedFrom":subQ0}),-1.0]])]});}
            var Q5;
            {var subQ5=sQuery(id+"F0.wireOp",EDGE,"E84.bottom");Q5=makeQuery(id+"F0.imprint","IMPRINT",FACE,{"disambiguationData":[TD([[makeQuery(id+"F0.imprint","IMPRINT",EDGE,{"derivedFrom":subQ5}),-1.0]])]});}
            var Q6;
            {var subQ0=sQuery(id+"F0.wireOp",EDGE,"E90");Q6=makeQuery(id+"F0.imprint","IMPRINT",FACE,{"disambiguationData":[TD([[makeQuery(id+"F0.imprint","IMPRINT",EDGE,{"derivedFrom":subQ0}),-1.0]])]});}
            var Q7;
            {var subQ0=sQuery(id+"F0.wireOp",EDGE,"E16");var subQ1=sQuery(id+"F0.wireOp",EDGE,"E14");var subQ2=makeQuery(id+"F0.imprint","INTERSECT",VERTEX,{"derivedFrom":[subQ1,subQ0]});Q7=makeQuery(id+"F0.imprint","IMPRINT",FACE,{"disambiguationData":[TD([[makeQuery(id+"F0.imprint","IMPRINT",EDGE,{"disambiguationData":[TD([[subQ2,1.0]])],"derivedFrom":subQ1}),-1.0]])]});}
            var Q8;
            {var subQ0=sQuery(id+"F0.wireOp",EDGE,"E17");var subQ1=sQuery(id+"F0.wireOp",EDGE,"E14");var subQ2=makeQuery(id+"F0.imprint","INTERSECT",VERTEX,{"derivedFrom":[subQ1,subQ0]});Q8=makeQuery(id+"F0.imprint","IMPRINT",FACE,{"disambiguationData":[TD([[makeQuery(id+"F0.imprint","IMPRINT",EDGE,{"disambiguationData":[TD([[subQ2,-1.0]])],"derivedFrom":subQ1}),-1.0]])]});}
            var Q9;
            {var subQ4=sQuery(id+"F0.wireOp",EDGE,"E75");Q9=makeQuery(id+"F0.imprint","IMPRINT",FACE,{"disambiguationData":[TD([[makeQuery(id+"F0.imprint","IMPRINT",EDGE,{"derivedFrom":subQ4}),1.0]])]});}
            var Q10;
            {var subQ0=sQuery(id+"F0.wireOp",EDGE,"E92.2");var subQ1=sQuery(id+"F0.wireOp",EDGE,"E65");var subQ2=makeQuery(id+"F0.imprint","INTERSECT",VERTEX,{"derivedFrom":[subQ1,subQ0]});Q10=makeQuery(id+"F0.imprint","IMPRINT",FACE,{"disambiguationData":[TD([[makeQuery(id+"F0.imprint","IMPRINT",EDGE,{"disambiguationData":[TD([[subQ2,-1.0]])],"derivedFrom":subQ1}),-1.0]])]});}
            var Q11;
            {var subQ1=sQuery(id+"F0.wireOp",EDGE,"E8");Q11=makeQuery(id+"F0.imprint","IMPRINT",FACE,{"disambiguationData":[TD([[makeQuery(id+"F0.imprint","IMPRINT",EDGE,{"derivedFrom":subQ1}),-1.0]])]});}
            var Q12;
            {var subQ0=sQuery(id+"F0.wireOp",EDGE,"E17");var subQ1=sQuery(id+"F0.wireOp",EDGE,"E14");var subQ2=makeQuery(id+"F0.imprint","INTERSECT",VERTEX,{"derivedFrom":[subQ1,subQ0]});Q12=makeQuery(id+"F0.imprint","IMPRINT",FACE,{"disambiguationData":[TD([[makeQuery(id+"F0.imprint","IMPRINT",EDGE,{"disambiguationData":[TD([[subQ2,-1.0]])],"derivedFrom":subQ1}),1.0]])]});}
            var Q13;
            {var subQ0=sQuery(id+"F0.wireOp",EDGE,"E94.MirrorCS");var subQ6=sQuery(id+"F0.wireOp",EDGE,"E68");var subQ11=makeQuery(id+"F0.imprint","INTERSECT",VERTEX,{"derivedFrom":[subQ6,subQ0]});Q13=makeQuery(id+"F0.imprint","IMPRINT",FACE,{"disambiguationData":[TD([[makeQuery(id+"F0.imprint","IMPRINT",EDGE,{"disambiguationData":[TD([[subQ11,-1.0]])],"derivedFrom":subQ6}),-1.0]])]});}
            var Q14;
            {var subQ5=sQuery(id+"F0.wireOp",EDGE,"E2");Q14=makeQuery(id+"F0.imprint","IMPRINT",FACE,{"disambiguationData":[TD([[makeQuery(id+"F0.imprint","IMPRINT",EDGE,{"derivedFrom":subQ5}),1.0]])]});}
            var Q15;
            {var subQ0=sQuery(id+"F0.wireOp",EDGE,"E83.left");Q15=makeQuery(id+"F0.imprint","IMPRINT",FACE,{"disambiguationData":[TD([[makeQuery(id+"F0.imprint","IMPRINT",EDGE,{"derivedFrom":subQ0}),1.0]])]});}
            var Q16;
            {var subQ13=sQuery(id+"F0.wireOp",EDGE,"E22");Q16=makeQuery(id+"F0.imprint","IMPRINT",FACE,{"disambiguationData":[TD([[makeQuery(id+"F0.imprint","IMPRINT",EDGE,{"derivedFrom":subQ13}),1.0]])]});}
            var Q17;
            {var subQ3=sQuery(id+"F0.wireOp",EDGE,"E81");var subQ7=sQuery(id+"F0.wireOp",EDGE,"E91.left");var subQ8=makeQuery(id+"F0.imprint","INTERSECT",VERTEX,{"derivedFrom":[subQ3,subQ7]});Q17=makeQuery(id+"F0.imprint","IMPRINT",FACE,{"disambiguationData":[TD([[makeQuery(id+"F0.imprint","IMPRINT",EDGE,{"disambiguationData":[TD([[subQ8,-1.0]])],"derivedFrom":subQ3}),1.0]])]});}
            var Q18;
            {var subQ5=sQuery(id+"F0.wireOp",EDGE,"E92.2");var subQ9=sQuery(id+"F0.wireOp",EDGE,"E65");var subQ10=makeQuery(id+"F0.imprint","INTERSECT",VERTEX,{"derivedFrom":[subQ9,subQ5]});Q18=makeQuery(id+"F0.imprint","IMPRINT",FACE,{"disambiguationData":[TD([[makeQuery(id+"F0.imprint","IMPRINT",EDGE,{"disambiguationData":[TD([[subQ10,-1.0]])],"derivedFrom":subQ9}),1.0]])]});}
            var Q19;
            {var subQ0=sQuery(id+"F0.wireOp",EDGE,"E14");var subQ1=makeQuery(id+"F0.imprint","IMPRINT",VERTEX,{"derivedFrom":subQ0});Q19=makeQuery(id+"F0.imprint","IMPRINT",FACE,{"disambiguationData":[TD([[makeQuery(id+"F0.imprint","IMPRINT",EDGE,{"disambiguationData":[TD([[subQ1,1.0]])],"derivedFrom":subQ0}),1.0]])]});}
            var Q20;
            {var subQ5=sQuery(id+"F0.wireOp",EDGE,"E87.top");Q20=makeQuery(id+"F0.imprint","IMPRINT",FACE,{"disambiguationData":[TD([[makeQuery(id+"F0.imprint","IMPRINT",EDGE,{"derivedFrom":subQ5}),-1.0]])]});}
            var Q21;
            {var subQ0=sQuery(id+"F0.wireOp",EDGE,"E3");var subQ5=sQuery(id+"F0.wireOp",EDGE,"E0.2");var subQ7=makeQuery(id+"F0.imprint","INTERSECT",VERTEX,{"derivedFrom":[subQ5,subQ0]});Q21=makeQuery(id+"F0.imprint","IMPRINT",FACE,{"disambiguationData":[TD([[makeQuery(id+"F0.imprint","IMPRINT",EDGE,{"disambiguationData":[TD([[subQ7,1.0]])],"derivedFrom":subQ0}),-1.0]])]});}
            var Q22;
            {var subQ0=sQuery(id+"F0.wireOp",EDGE,"E92.0");var subQ1=sQuery(id+"F0.wireOp",EDGE,"E81");var subQ2=makeQuery(id+"F0.imprint","INTERSECT",VERTEX,{"derivedFrom":[subQ1,subQ0]});Q22=makeQuery(id+"F0.imprint","IMPRINT",FACE,{"disambiguationData":[TD([[makeQuery(id+"F0.imprint","IMPRINT",EDGE,{"disambiguationData":[TD([[subQ2,-1.0]])],"derivedFrom":subQ1}),1.0]])]});}
            var Q23;
            {var subQ4=sQuery(id+"F0.wireOp",EDGE,"E71");Q23=makeQuery(id+"F0.imprint","IMPRINT",FACE,{"disambiguationData":[TD([[makeQuery(id+"F0.imprint","IMPRINT",EDGE,{"derivedFrom":subQ4}),-1.0]])]});}
            var Q24;
            {var subQ21=sQuery(id+"F0.wireOp",EDGE,"E22");Q24=makeQuery(id+"F0.imprint","IMPRINT",FACE,{"disambiguationData":[TD([[makeQuery(id+"F0.imprint","IMPRINT",EDGE,{"derivedFrom":subQ21}),-1.0]])]});}
            var Q25;
            {var subQ8=sQuery(id+"F0.wireOp",EDGE,"E75");Q25=makeQuery(id+"F0.imprint","IMPRINT",FACE,{"disambiguationData":[TD([[makeQuery(id+"F0.imprint","IMPRINT",EDGE,{"derivedFrom":subQ8}),-1.0]])]});}
            var Q26;
            {var subQ4=sQuery(id+"F0.wireOp",EDGE,"E5");var subQ8=sQuery(id+"F0.wireOp",EDGE,"E0.1");var subQ9=makeQuery(id+"F0.imprint","INTERSECT",VERTEX,{"derivedFrom":[subQ8,subQ4]});Q26=makeQuery(id+"F0.imprint","IMPRINT",FACE,{"disambiguationData":[TD([[makeQuery(id+"F0.imprint","IMPRINT",EDGE,{"disambiguationData":[TD([[subQ9,-1.0]])],"derivedFrom":subQ8}),-1.0]])]});}
            var Q27;
            {var subQ0=sQuery(id+"F0.wireOp",EDGE,"E16");var subQ1=sQuery(id+"F0.wireOp",EDGE,"E14");var subQ2=makeQuery(id+"F0.imprint","INTERSECT",VERTEX,{"derivedFrom":[subQ1,subQ0]});Q27=makeQuery(id+"F0.imprint","IMPRINT",FACE,{"disambiguationData":[TD([[makeQuery(id+"F0.imprint","IMPRINT",EDGE,{"disambiguationData":[TD([[subQ2,1.0]])],"derivedFrom":subQ1}),1.0]])]});}
            var Q28;
            {var subQ8=sQuery(id+"F0.wireOp",EDGE,"E71");Q28=makeQuery(id+"F0.imprint","IMPRINT",FACE,{"disambiguationData":[TD([[makeQuery(id+"F0.imprint","IMPRINT",EDGE,{"derivedFrom":subQ8}),1.0]])]});}
            var Q29;
            {var subQ0=sQuery(id+"F0.wireOp",EDGE,"E15");var subQ1=sQuery(id+"F0.wireOp",EDGE,"E14");var subQ2=makeQuery(id+"F0.imprint","INTERSECT",VERTEX,{"derivedFrom":[subQ1,subQ0]});Q29=makeQuery(id+"F0.imprint","IMPRINT",FACE,{"disambiguationData":[TD([[makeQuery(id+"F0.imprint","IMPRINT",EDGE,{"disambiguationData":[TD([[subQ2,-1.0]])],"derivedFrom":subQ1}),1.0]])]});}
            var Q30;
            {var subQ0=sQuery(id+"F0.wireOp",EDGE,"E15");var subQ1=sQuery(id+"F0.wireOp",EDGE,"E14");var subQ2=makeQuery(id+"F0.imprint","INTERSECT",VERTEX,{"derivedFrom":[subQ1,subQ0]});Q30=makeQuery(id+"F0.imprint","IMPRINT",FACE,{"disambiguationData":[TD([[makeQuery(id+"F0.imprint","IMPRINT",EDGE,{"disambiguationData":[TD([[subQ2,-1.0]])],"derivedFrom":subQ1}),-1.0]])]});}
            var Q31;
            {var subQ0=sQuery(id+"F0.wireOp",EDGE,"E94.MirrorCS");var subQ1=sQuery(id+"F0.wireOp",EDGE,"E68");var subQ2=makeQuery(id+"F0.imprint","INTERSECT",VERTEX,{"derivedFrom":[subQ1,subQ0]});Q31=makeQuery(id+"F0.imprint","IMPRINT",FACE,{"disambiguationData":[TD([[makeQuery(id+"F0.imprint","IMPRINT",EDGE,{"disambiguationData":[TD([[subQ2,-1.0]])],"derivedFrom":subQ1}),1.0]])]});}
            var Q32;
            {var subQ7=sQuery(id+"F0.wireOp",EDGE,"E89.bottom");Q32=makeQuery(id+"F0.imprint","IMPRINT",FACE,{"disambiguationData":[TD([[makeQuery(id+"F0.imprint","IMPRINT",EDGE,{"derivedFrom":subQ7}),1.0]])]});}
            var Q33;
            {var subQ1=sQuery(id+"F0.wireOp",EDGE,"E4");Q33=makeQuery(id+"F0.imprint","IMPRINT",FACE,{"disambiguationData":[TD([[makeQuery(id+"F0.imprint","IMPRINT",EDGE,{"derivedFrom":subQ1}),1.0]])]});}
            var Q34;
            {var subQ0=sQuery(id+"F0.wireOp",EDGE,"E63");var subQ1=sQuery(id+"F0.wireOp",EDGE,"E0.1");var subQ2=makeQuery(id+"F0.imprint","INTERSECT",VERTEX,{"derivedFrom":[subQ1,subQ0]});Q34=makeQuery(id+"F0.imprint","IMPRINT",FACE,{"disambiguationData":[TD([[makeQuery(id+"F0.imprint","IMPRINT",EDGE,{"disambiguationData":[TD([[subQ2,1.0]])],"derivedFrom":subQ1}),-1.0]])]});}
            var Q35;
            {var subQ0=sQuery(id+"F0.wireOp",EDGE,"E65");var subQ1=sQuery(id+"F0.wireOp",EDGE,"E0.2");var subQ2=makeQuery(id+"F0.imprint","INTERSECT",VERTEX,{"derivedFrom":[subQ1,subQ0]});Q35=makeQuery(id+"F0.imprint","IMPRINT",FACE,{"disambiguationData":[TD([[makeQuery(id+"F0.imprint","IMPRINT",EDGE,{"disambiguationData":[TD([[subQ2,1.0]])],"derivedFrom":subQ1}),-1.0]])]});}
            var Q36;
            {var subQ14=sQuery(id+"F0.wireOp",EDGE,"E88.bottom");Q36=makeQuery(id+"F0.imprint","IMPRINT",FACE,{"disambiguationData":[TD([[makeQuery(id+"F0.imprint","IMPRINT",EDGE,{"derivedFrom":subQ14}),1.0]])]});}
            var Q37;
            {var subQ0=sQuery(id+"F0.wireOp",EDGE,"E3");var subQ1=sQuery(id+"F0.wireOp",EDGE,"E0.2");var subQ2=makeQuery(id+"F0.imprint","INTERSECT",VERTEX,{"derivedFrom":[subQ1,subQ0]});Q37=makeQuery(id+"F0.imprint","IMPRINT",FACE,{"disambiguationData":[TD([[makeQuery(id+"F0.imprint","IMPRINT",EDGE,{"disambiguationData":[TD([[subQ2,-1.0]])],"derivedFrom":subQ1}),1.0]])]});}
            var Q38;
            {var subQ1=sQuery(id+"F0.wireOp",EDGE,"E81");var subQ5=sQuery(id+"F0.wireOp",EDGE,"E88.left");var subQ8=makeQuery(id+"F0.imprint","INTERSECT",VERTEX,{"derivedFrom":[subQ1,subQ5]});Q38=makeQuery(id+"F0.imprint","IMPRINT",FACE,{"disambiguationData":[TD([[makeQuery(id+"F0.imprint","IMPRINT",EDGE,{"disambiguationData":[TD([[subQ8,-1.0]])],"derivedFrom":subQ1}),1.0]])]});}
            var Q39;
            {var subQ7=sQuery(id+"F0.wireOp",EDGE,"E90");Q39=makeQuery(id+"F0.imprint","IMPRINT",FACE,{"disambiguationData":[TD([[makeQuery(id+"F0.imprint","IMPRINT",EDGE,{"derivedFrom":subQ7}),1.0]])]});}
            var Q40;
            {var subQ0=sQuery(id+"F0.wireOp",EDGE,"E95.MirrorCS");var subQ1=sQuery(id+"F0.wireOp",EDGE,"E81");var subQ2=makeQuery(id+"F0.imprint","INTERSECT",VERTEX,{"derivedFrom":[subQ1,subQ0]});Q40=makeQuery(id+"F0.imprint","IMPRINT",FACE,{"disambiguationData":[TD([[makeQuery(id+"F0.imprint","IMPRINT",EDGE,{"disambiguationData":[TD([[subQ2,-1.0]])],"derivedFrom":subQ1}),1.0]])]});}
            var Q41;
            {var subQ1=sQuery(id+"F0.wireOp",EDGE,"E18.0");Q41=makeQuery(id+"F0.imprint","IMPRINT",FACE,{"disambiguationData":[TD([[makeQuery(id+"F0.imprint","IMPRINT",EDGE,{"derivedFrom":subQ1}),-1.0]])]});}
            var Q42;
            {var subQ0=sQuery(id+"F0.wireOp",EDGE,"E63");var subQ1=sQuery(id+"F0.wireOp",EDGE,"E0.2");var subQ2=makeQuery(id+"F0.imprint","INTERSECT",VERTEX,{"derivedFrom":[subQ1,subQ0]});Q42=makeQuery(id+"F0.imprint","IMPRINT",FACE,{"disambiguationData":[TD([[makeQuery(id+"F0.imprint","IMPRINT",EDGE,{"disambiguationData":[TD([[subQ2,-1.0]])],"derivedFrom":subQ1}),-1.0]])]});}
            var Q43;
            {var subQ0=sQuery(id+"F0.wireOp",EDGE,"E5");var subQ1=sQuery(id+"F0.wireOp",EDGE,"E0.1");var subQ2=makeQuery(id+"F0.imprint","INTERSECT",VERTEX,{"derivedFrom":[subQ1,subQ0]});Q43=makeQuery(id+"F0.imprint","IMPRINT",FACE,{"disambiguationData":[TD([[makeQuery(id+"F0.imprint","IMPRINT",EDGE,{"disambiguationData":[TD([[subQ2,-1.0]])],"derivedFrom":subQ1}),1.0]])]});}
            var Q44;
            {var subQ0=sQuery(id+"F0.wireOp",EDGE,"E14");var subQ1=makeQuery(id+"F0.imprint","IMPRINT",VERTEX,{"derivedFrom":subQ0});Q44=makeQuery(id+"F0.imprint","IMPRINT",FACE,{"disambiguationData":[TD([[makeQuery(id+"F0.imprint","IMPRINT",EDGE,{"disambiguationData":[TD([[subQ1,1.0]])],"derivedFrom":subQ0}),-1.0]])]});}
            var Q45;
            Q45=makeQuery(id+"F0.imprint","IMPRINT",FACE,{"disambiguationData":[TD([[makeQuery(id+"F0.imprint","IMPRINT",EDGE,{"derivedFrom":sQuery(id+"F0.wireOp",EDGE,"E49.MirrorCS")}),1.0]])]});
            var Q46;
            Q46=makeQuery(id+"F0.imprint","IMPRINT",FACE,{"disambiguationData":[TD([[makeQuery(id+"F0.imprint","IMPRINT",EDGE,{"derivedFrom":sQuery(id+"F0.wireOp",EDGE,"E43.MirrorCS")}),-1.0]])]});
            var Q47;
            Q47=makeQuery(id+"F0.imprint","IMPRINT",FACE,{"disambiguationData":[TD([[makeQuery(id+"F0.imprint","IMPRINT",EDGE,{"derivedFrom":sQuery(id+"F0.wireOp",EDGE,"E37.MirrorCS")}),-1.0]])]});
            var Q48;
            {var subQ0=sQuery(id+"F0.wireOp",EDGE,"E34");Q48=makeQuery(id+"F0.imprint","IMPRINT",FACE,{"disambiguationData":[TD([[makeQuery(id+"F0.imprint","IMPRINT",EDGE,{"derivedFrom":subQ0}),1.0]])]});}
            var Q49;
            {var subQ5=sQuery(id+"F0.wireOp",EDGE,"E88.top");Q49=makeQuery(id+"F0.imprint","IMPRINT",FACE,{"disambiguationData":[TD([[makeQuery(id+"F0.imprint","IMPRINT",EDGE,{"derivedFrom":subQ5}),1.0]])]});}
            var Q50;
            Q50=makeQuery(id+"F0.imprint","IMPRINT",FACE,{"disambiguationData":[TD([[makeQuery(id+"F0.imprint","IMPRINT",EDGE,{"derivedFrom":sQuery(id+"F0.wireOp",EDGE,"E85.bottom")}),1.0]])]});
            var Q51;
            {var subQ5=sQuery(id+"F0.wireOp",EDGE,"E89.bottom");Q51=makeQuery(id+"F0.imprint","IMPRINT",FACE,{"disambiguationData":[TD([[makeQuery(id+"F0.imprint","IMPRINT",EDGE,{"derivedFrom":subQ5}),-1.0]])]});}
            var Q52;
            {var subQ5=sQuery(id+"F0.wireOp",EDGE,"E86.bottom");Q52=makeQuery(id+"F0.imprint","IMPRINT",FACE,{"disambiguationData":[TD([[makeQuery(id+"F0.imprint","IMPRINT",EDGE,{"derivedFrom":subQ5}),-1.0]])]});}
            var Q53;
            {var subQ5=sQuery(id+"F0.wireOp",EDGE,"E89.top");Q53=makeQuery(id+"F0.imprint","IMPRINT",FACE,{"disambiguationData":[TD([[makeQuery(id+"F0.imprint","IMPRINT",EDGE,{"derivedFrom":subQ5}),1.0]])]});}
            var Q54;
            Q54=makeQuery(id+"F0.imprint","IMPRINT",FACE,{"disambiguationData":[TD([[makeQuery(id+"F0.imprint","IMPRINT",EDGE,{"derivedFrom":sQuery(id+"F0.wireOp",EDGE,"E83.bottom")}),1.0]])]});
            var Q55;
            {var subQ5=sQuery(id+"F0.wireOp",EDGE,"E91.top");Q55=makeQuery(id+"F0.imprint","IMPRINT",FACE,{"disambiguationData":[TD([[makeQuery(id+"F0.imprint","IMPRINT",EDGE,{"derivedFrom":subQ5}),1.0]])]});}
            var Q56;
            {var subQ5=sQuery(id+"F0.wireOp",EDGE,"E87.top");Q56=makeQuery(id+"F0.imprint","IMPRINT",FACE,{"disambiguationData":[TD([[makeQuery(id+"F0.imprint","IMPRINT",EDGE,{"derivedFrom":subQ5}),1.0]])]});}
            var Q57;
            {var subQ0=sQuery(id+"F0.wireOp",EDGE,"E91.right");var subQ6=sQuery(id+"F0.wireOp",EDGE,"E81");var subQ8=makeQuery(id+"F0.imprint","INTERSECT",VERTEX,{"derivedFrom":[subQ6,subQ0]});Q57=makeQuery(id+"F0.imprint","IMPRINT",FACE,{"disambiguationData":[TD([[makeQuery(id+"F0.imprint","IMPRINT",EDGE,{"disambiguationData":[TD([[subQ8,-1.0]])],"derivedFrom":subQ6}),-1.0]])]});}
            var Q58;
            {var subQ5=sQuery(id+"F0.wireOp",EDGE,"E86.top");Q58=makeQuery(id+"F0.imprint","IMPRINT",FACE,{"disambiguationData":[TD([[makeQuery(id+"F0.imprint","IMPRINT",EDGE,{"derivedFrom":subQ5}),1.0]])]});}
            var Q59;
            Q59=makeQuery(id+"F0.imprint","IMPRINT",FACE,{"disambiguationData":[TD([[makeQuery(id+"F0.imprint","IMPRINT",EDGE,{"derivedFrom":sQuery(id+"F0.wireOp",EDGE,"E84.bottom")}),1.0]])]});
            var Q60;
            {var subQ5=sQuery(id+"F0.wireOp",EDGE,"E87.bottom");Q60=makeQuery(id+"F0.imprint","IMPRINT",FACE,{"disambiguationData":[TD([[makeQuery(id+"F0.imprint","IMPRINT",EDGE,{"derivedFrom":subQ5}),-1.0]])]});}
            var Q61;
            Q61=makeQuery(id+"F0.imprint","IMPRINT",FACE,{"disambiguationData":[TD([[makeQuery(id+"F0.imprint","IMPRINT",EDGE,{"derivedFrom":sQuery(id+"F0.wireOp",EDGE,"E52.MirrorCS")}),-1.0]])]});
            var Q62;
            Q62=makeQuery(id+"F0.imprint","IMPRINT",FACE,{"disambiguationData":[TD([[makeQuery(id+"F0.imprint","IMPRINT",EDGE,{"derivedFrom":sQuery(id+"F0.wireOp",EDGE,"E29.MirrorCS")}),1.0]])]});
            var Q63;
            Q63=makeQuery(id+"F0.imprint","IMPRINT",FACE,{"disambiguationData":[TD([[makeQuery(id+"F0.imprint","IMPRINT",EDGE,{"derivedFrom":sQuery(id+"F0.wireOp",EDGE,"E45.MirrorCS")}),1.0]])]});
            var Q64;
            {var subQ0=sQuery(id+"F0.wireOp",EDGE,"E26");Q64=makeQuery(id+"F0.imprint","IMPRINT",FACE,{"disambiguationData":[TD([[makeQuery(id+"F0.imprint","IMPRINT",EDGE,{"derivedFrom":subQ0}),-1.0]])]});}
            var Q65;
            {var subQ0=sQuery(id+"F0.wireOp",EDGE,"E93.MirrorCS");var subQ1=sQuery(id+"F0.wireOp",EDGE,"E81");var subQ2=makeQuery(id+"F0.imprint","INTERSECT",VERTEX,{"derivedFrom":[subQ1,subQ0]});Q65=makeQuery(id+"F0.imprint","IMPRINT",FACE,{"disambiguationData":[TD([[makeQuery(id+"F0.imprint","IMPRINT",EDGE,{"disambiguationData":[TD([[subQ2,-1.0]])],"derivedFrom":subQ1}),-1.0]])]});}
            var Q66;
            {var subQ1=sQuery(id+"F0.wireOp",EDGE,"E68");var subQ3=sQuery(id+"F0.wireOp",EDGE,"E94.MirrorCS");var subQ4=makeQuery(id+"F0.imprint","INTERSECT",VERTEX,{"derivedFrom":[subQ1,subQ3]});Q66=makeQuery(id+"F0.imprint","IMPRINT",FACE,{"disambiguationData":[TD([[makeQuery(id+"F0.imprint","IMPRINT",EDGE,{"disambiguationData":[TD([[subQ4,-1.0]])],"derivedFrom":subQ3}),-1.0]])]});}
            var Q67;
            {var subQ0=sQuery(id+"F0.wireOp",EDGE,"E94.MirrorCS");var subQ1=sQuery(id+"F0.wireOp",EDGE,"E88.right");var subQ2=makeQuery(id+"F0.imprint","INTERSECT",VERTEX,{"derivedFrom":[subQ1,subQ0]});Q67=makeQuery(id+"F0.imprint","IMPRINT",FACE,{"disambiguationData":[TD([[makeQuery(id+"F0.imprint","IMPRINT",EDGE,{"disambiguationData":[TD([[subQ2,-1.0]])],"derivedFrom":subQ1}),-1.0]])]});}
            var Q68;
            {var subQ0=sQuery(id+"F0.wireOp",EDGE,"E88.right");var subQ1=sQuery(id+"F0.wireOp",EDGE,"E81");var subQ2=makeQuery(id+"F0.imprint","INTERSECT",VERTEX,{"derivedFrom":[subQ1,subQ0]});Q68=makeQuery(id+"F0.imprint","IMPRINT",FACE,{"disambiguationData":[TD([[makeQuery(id+"F0.imprint","IMPRINT",EDGE,{"disambiguationData":[TD([[subQ2,-1.0]])],"derivedFrom":subQ1}),-1.0]])]});}
            var Q69;
            {var subQ1=sQuery(id+"F0.wireOp",EDGE,"E65");var subQ3=sQuery(id+"F0.wireOp",EDGE,"E92.2");var subQ4=makeQuery(id+"F0.imprint","INTERSECT",VERTEX,{"derivedFrom":[subQ1,subQ3]});Q69=makeQuery(id+"F0.imprint","IMPRINT",FACE,{"disambiguationData":[TD([[makeQuery(id+"F0.imprint","IMPRINT",EDGE,{"disambiguationData":[TD([[subQ4,-1.0]])],"derivedFrom":subQ3}),1.0]])]});}
            var Q70;
            {var subQ1=sQuery(id+"F0.wireOp",EDGE,"E88.bottom");Q70=makeQuery(id+"F0.imprint","IMPRINT",FACE,{"disambiguationData":[TD([[makeQuery(id+"F0.imprint","IMPRINT",EDGE,{"derivedFrom":subQ1}),-1.0]])]});}
            var Q71;
            {var subQ0=sQuery(id+"F0.wireOp",EDGE,"E92.2");var subQ1=sQuery(id+"F0.wireOp",EDGE,"E88.left");var subQ2=makeQuery(id+"F0.imprint","INTERSECT",VERTEX,{"derivedFrom":[subQ1,subQ0]});Q71=makeQuery(id+"F0.imprint","IMPRINT",FACE,{"disambiguationData":[TD([[makeQuery(id+"F0.imprint","IMPRINT",EDGE,{"disambiguationData":[TD([[subQ2,-1.0]])],"derivedFrom":subQ1}),1.0]])]});}
            var Q72;
            {var subQ0=sQuery(id+"F0.wireOp",EDGE,"E88.left");var subQ1=sQuery(id+"F0.wireOp",EDGE,"E81");var subQ2=makeQuery(id+"F0.imprint","INTERSECT",VERTEX,{"derivedFrom":[subQ1,subQ0]});Q72=makeQuery(id+"F0.imprint","IMPRINT",FACE,{"disambiguationData":[TD([[makeQuery(id+"F0.imprint","IMPRINT",EDGE,{"disambiguationData":[TD([[subQ2,-1.0]])],"derivedFrom":subQ1}),-1.0]])]});}
            extrude(context, id + "F4", {"entities" : qUnion([Q0, Q1, Q2, Q3, Q4, Q5, Q6, Q7, Q8, Q9, Q10, Q11, Q12, Q13, Q14, Q15, Q16, Q17, Q18, Q19, Q20, Q21, Q22, Q23, Q24, Q25, Q26, Q27, Q28, Q29, Q30, Q31, Q32, Q33, Q34, Q35, Q36, Q37, Q38, Q39, Q40, Q41, Q42, Q43, Q44, Q45, Q46, Q47, Q48, Q49, Q50, Q51, Q52, Q53, Q54, Q55, Q56, Q57, Q58, Q59, Q60, Q61, Q62, Q63, Q64, Q65, Q66, Q67, Q68, Q69, Q70, Q71, Q72]), "oppositeDirection" : true, "depth" : 1 * mm, "offsetDistance" : 25 * mm});
        }
        {
            var Q0;
            {var subQ0=sQuery(id+"F0.wireOp",EDGE,"E0.1");Q0=makeQuery(id+"F2.opExtrude","CAP_EDGE",EDGE,{"disambiguationData":[OSD([subQ0]),TDD([makeQuery(id+"F0.imprint","IMPRINT",EDGE,{"disambiguationData":[TD([[makeQuery(id+"F0.imprint","INTERSECT",VERTEX,{"derivedFrom":[subQ0,sQuery(id+"F0.wireOp",EDGE,"E82")]}),-1.0]])],"derivedFrom":subQ0})])],"isStart":false});}
            var Q1;
            Q1=makeQuery(id+"F2.opExtrude","CAP_EDGE",EDGE,{"disambiguationData":[OSD([sQuery(id+"F0.wireOp",EDGE,"E18.2")])],"isStart":false});
            var Q2;
            {var subQ0=sQuery(id+"F0.wireOp",EDGE,"E63");Q2=makeQuery(id+"F2.opExtrude","CAP_EDGE",EDGE,{"disambiguationData":[OSD([subQ0]),TDD([makeQuery(id+"F0.imprint","IMPRINT",EDGE,{"disambiguationData":[TD([[makeQuery(id+"F0.imprint","INTERSECT",VERTEX,{"derivedFrom":[sQuery(id+"F0.wireOp",EDGE,"E0.1"),subQ0]}),-1.0]])],"derivedFrom":subQ0})])],"isStart":false});}
            var Q3;
            {var subQ0=sQuery(id+"F0.wireOp",EDGE,"E0.1");Q3=makeQuery(id+"F2.opExtrude","CAP_EDGE",EDGE,{"disambiguationData":[OSD([subQ0]),TDD([makeQuery(id+"F0.imprint","IMPRINT",EDGE,{"disambiguationData":[TD([[makeQuery(id+"F0.imprint","INTERSECT",VERTEX,{"derivedFrom":[subQ0,sQuery(id+"F0.wireOp",EDGE,"E63")]}),1.0]])],"derivedFrom":subQ0})])],"isStart":false});}
            var Q4;
            {var subQ0=sQuery(id+"F0.wireOp",EDGE,"E0.1");Q4=makeQuery(id+"F2.opExtrude","CAP_EDGE",EDGE,{"disambiguationData":[OSD([subQ0]),TDD([makeQuery(id+"F0.imprint","IMPRINT",EDGE,{"disambiguationData":[TD([[makeQuery(id+"F0.imprint","INTERSECT",VERTEX,{"derivedFrom":[subQ0,sQuery(id+"F0.wireOp",EDGE,"E68")]}),1.0]])],"derivedFrom":subQ0})])],"isStart":false});}
            var Q5;
            {var subQ0=sQuery(id+"F0.wireOp",EDGE,"E0.1");Q5=makeQuery(id+"F2.opExtrude","CAP_EDGE",EDGE,{"disambiguationData":[OSD([subQ0]),TDD([makeQuery(id+"F0.imprint","IMPRINT",EDGE,{"disambiguationData":[TD([[makeQuery(id+"F0.imprint","INTERSECT",VERTEX,{"derivedFrom":[sQuery(id+"F0.wireOp",EDGE,"E0.0"),subQ0]}),-1.0]])],"derivedFrom":subQ0})])],"isStart":false});}
            var Q6;
            Q6=makeQuery(id+"F2.opExtrude","CAP_EDGE",EDGE,{"disambiguationData":[OSD([sQuery(id+"F0.wireOp",EDGE,"E71")])],"isStart":false});
            var Q7;
            Q7=makeQuery(id+"F2.opExtrude","CAP_EDGE",EDGE,{"disambiguationData":[OSD([sQuery(id+"F0.wireOp",EDGE,"E68"),sQuery(id+"F0.wireOp",EDGE,"E90"),sQuery(id+"F0.wireOp",EDGE,"E91.bottom")])],"isStart":false});
            var Q8;
            Q8=makeQuery(id+"F2.opExtrude","CAP_EDGE",EDGE,{"disambiguationData":[OSD([sQuery(id+"F0.wireOp",EDGE,"E91.right")])],"isStart":false});
            var Q9;
            Q9=makeQuery(id+"F2.opExtrude","CAP_EDGE",EDGE,{"disambiguationData":[OSD([sQuery(id+"F0.wireOp",EDGE,"E91.left")])],"isStart":false});
            var Q10;
            {var subQ0=sQuery(id+"F0.wireOp",EDGE,"E63");Q10=makeQuery(id+"F2.opExtrude","CAP_EDGE",EDGE,{"disambiguationData":[OSD([subQ0]),TDD([makeQuery(id+"F0.imprint","IMPRINT",EDGE,{"disambiguationData":[TD([[makeQuery(id+"F0.imprint","INTERSECT",VERTEX,{"derivedFrom":[subQ0,sQuery(id+"F0.wireOp",EDGE,"E88.top"),sQuery(id+"F0.wireOp",EDGE,"E88.right")]}),1.0]])],"derivedFrom":subQ0})])],"isStart":false});}
            var Q11;
            Q11=makeQuery(id+"F2.opExtrude","CAP_EDGE",EDGE,{"disambiguationData":[OSD([sQuery(id+"F0.wireOp",EDGE,"E88.left")])],"isStart":false});
            var Q12;
            Q12=makeQuery(id+"F2.opExtrude","CAP_EDGE",EDGE,{"disambiguationData":[OSD([sQuery(id+"F0.wireOp",EDGE,"E88.right")])],"isStart":false});
            var Q13;
            Q13=makeQuery(id+"F2.opExtrude","CAP_EDGE",EDGE,{"disambiguationData":[OSD([sQuery(id+"F0.wireOp",EDGE,"E65"),sQuery(id+"F0.wireOp",EDGE,"E68"),sQuery(id+"F0.wireOp",EDGE,"E88.bottom")])],"isStart":false});
            var Q14;
            {var subQ0=sQuery(id+"F0.wireOp",EDGE,"E81");Q14=makeQuery(id+"F2.opExtrude","CAP_EDGE",EDGE,{"disambiguationData":[OSD([subQ0]),TDD([makeQuery(id+"F0.imprint","IMPRINT",EDGE,{"disambiguationData":[TD([[makeQuery(id+"F0.imprint","INTERSECT",VERTEX,{"derivedFrom":[subQ0,sQuery(id+"F0.wireOp",EDGE,"E93.MirrorCS")]}),-1.0]])],"derivedFrom":subQ0})])],"isStart":false});}
            var Q15;
            {var subQ0=sQuery(id+"F0.wireOp",EDGE,"E81");Q15=makeQuery(id+"F2.opExtrude","CAP_EDGE",EDGE,{"disambiguationData":[OSD([subQ0]),TDD([makeQuery(id+"F0.imprint","IMPRINT",EDGE,{"disambiguationData":[TD([[makeQuery(id+"F0.imprint","INTERSECT",VERTEX,{"derivedFrom":[subQ0,sQuery(id+"F0.wireOp",EDGE,"E88.left")]}),-1.0]])],"derivedFrom":subQ0})])],"isStart":false});}
            var Q16;
            {var subQ0=sQuery(id+"F0.wireOp",EDGE,"E63");Q16=makeQuery(id+"F2.opExtrude","CAP_EDGE",EDGE,{"disambiguationData":[OSD([subQ0]),TDD([makeQuery(id+"F0.imprint","IMPRINT",EDGE,{"disambiguationData":[TD([[makeQuery(id+"F0.imprint","INTERSECT",VERTEX,{"derivedFrom":[subQ0,sQuery(id+"F0.wireOp",EDGE,"E88.top"),sQuery(id+"F0.wireOp",EDGE,"E88.left")]}),-1.0]])],"derivedFrom":subQ0})])],"isStart":false});}
            var Q17;
            Q17=makeQuery(id+"F2.opExtrude","CAP_EDGE",EDGE,{"disambiguationData":[OSD([sQuery(id+"F0.wireOp",EDGE,"E82")])],"isStart":false});
            var Q18;
            Q18=makeQuery(id+"F2.opExtrude","CAP_EDGE",EDGE,{"disambiguationData":[OSD([sQuery(id+"F0.wireOp",EDGE,"E18.1")])],"isStart":false});
            var Q19;
            {var subQ0=sQuery(id+"F0.wireOp",EDGE,"E0.2");Q19=makeQuery(id+"F2.opExtrude","CAP_EDGE",EDGE,{"disambiguationData":[OSD([subQ0]),TDD([makeQuery(id+"F0.imprint","IMPRINT",EDGE,{"disambiguationData":[TD([[makeQuery(id+"F0.imprint","INTERSECT",VERTEX,{"derivedFrom":[subQ0,sQuery(id+"F0.wireOp",EDGE,"E82")]}),1.0]])],"derivedFrom":subQ0})])],"isStart":false});}
            var Q20;
            Q20=makeQuery(id+"F2.opExtrude","CAP_EDGE",EDGE,{"disambiguationData":[OSD([sQuery(id+"F0.wireOp",EDGE,"E89.right")])],"isStart":false});
            var Q21;
            Q21=makeQuery(id+"F2.opExtrude","CAP_EDGE",EDGE,{"disambiguationData":[OSD([sQuery(id+"F0.wireOp",EDGE,"E89.left")])],"isStart":false});
            var Q22;
            {var subQ0=sQuery(id+"F0.wireOp",EDGE,"E63");Q22=makeQuery(id+"F2.opExtrude","CAP_EDGE",EDGE,{"disambiguationData":[OSD([subQ0]),TDD([makeQuery(id+"F0.imprint","IMPRINT",EDGE,{"disambiguationData":[TD([[makeQuery(id+"F0.imprint","INTERSECT",VERTEX,{"derivedFrom":[sQuery(id+"F0.wireOp",EDGE,"E0.2"),subQ0]}),1.0]])],"derivedFrom":subQ0})])],"isStart":false});}
            var Q23;
            {var subQ0=sQuery(id+"F0.wireOp",EDGE,"E0.2");Q23=makeQuery(id+"F2.opExtrude","CAP_EDGE",EDGE,{"disambiguationData":[OSD([subQ0]),TDD([makeQuery(id+"F0.imprint","IMPRINT",EDGE,{"disambiguationData":[TD([[makeQuery(id+"F0.imprint","INTERSECT",VERTEX,{"derivedFrom":[subQ0,sQuery(id+"F0.wireOp",EDGE,"E63")]}),-1.0]])],"derivedFrom":subQ0})])],"isStart":false});}
            var Q24;
            {var subQ0=sQuery(id+"F0.wireOp",EDGE,"E0.2");Q24=makeQuery(id+"F2.opExtrude","CAP_EDGE",EDGE,{"disambiguationData":[OSD([subQ0]),TDD([makeQuery(id+"F0.imprint","IMPRINT",EDGE,{"disambiguationData":[TD([[makeQuery(id+"F0.imprint","INTERSECT",VERTEX,{"derivedFrom":[subQ0,sQuery(id+"F0.wireOp",EDGE,"E65")]}),-1.0]])],"derivedFrom":subQ0})])],"isStart":false});}
            var Q25;
            {var subQ0=sQuery(id+"F0.wireOp",EDGE,"E0.2");Q25=makeQuery(id+"F2.opExtrude","CAP_EDGE",EDGE,{"disambiguationData":[OSD([subQ0]),TDD([makeQuery(id+"F0.imprint","IMPRINT",EDGE,{"disambiguationData":[TD([[makeQuery(id+"F0.imprint","INTERSECT",VERTEX,{"derivedFrom":[sQuery(id+"F0.wireOp",EDGE,"E0.0"),subQ0]}),1.0]])],"derivedFrom":subQ0})])],"isStart":false});}
            var Q26;
            Q26=makeQuery(id+"F2.opExtrude","CAP_EDGE",EDGE,{"disambiguationData":[OSD([sQuery(id+"F0.wireOp",EDGE,"E18.0")])],"isStart":false});
            var Q27;
            Q27=makeQuery(id+"F2.opExtrude","CAP_EDGE",EDGE,{"disambiguationData":[OSD([sQuery(id+"F0.wireOp",EDGE,"E75")])],"isStart":false});
            var Q28;
            Q28=makeQuery(id+"F2.opExtrude","CAP_EDGE",EDGE,{"disambiguationData":[OSD([sQuery(id+"F0.wireOp",EDGE,"E65"),sQuery(id+"F0.wireOp",EDGE,"E89.bottom")])],"isStart":false});
            var Q29;
            Q29=makeQuery(id+"F2.opExtrude","CAP_EDGE",EDGE,{"disambiguationData":[OSD([sQuery(id+"F0.wireOp",EDGE,"E65")])],"isStart":false});
            var Q30;
            {var subQ0=sQuery(id+"F0.wireOp",EDGE,"E81");Q30=makeQuery(id+"F2.opExtrude","CAP_EDGE",EDGE,{"disambiguationData":[OSD([subQ0]),TDD([makeQuery(id+"F0.imprint","IMPRINT",EDGE,{"disambiguationData":[TD([[makeQuery(id+"F0.imprint","INTERSECT",VERTEX,{"derivedFrom":[subQ0,sQuery(id+"F0.wireOp",EDGE,"E92.1")]}),-1.0]])],"derivedFrom":subQ0})])],"isStart":false});}
            var Q31;
            {var subQ0=sQuery(id+"F0.wireOp",EDGE,"E81");Q31=makeQuery(id+"F2.opExtrude","CAP_EDGE",EDGE,{"disambiguationData":[OSD([subQ0]),TDD([makeQuery(id+"F0.imprint","IMPRINT",EDGE,{"disambiguationData":[TD([[makeQuery(id+"F0.imprint","INTERSECT",VERTEX,{"derivedFrom":[subQ0,sQuery(id+"F0.wireOp",EDGE,"E91.left")]}),-1.0]])],"derivedFrom":subQ0})])],"isStart":false});}
            var Q32;
            {var subQ0=sQuery(id+"F0.wireOp",EDGE,"E81");Q32=makeQuery(id+"F2.opExtrude","CAP_EDGE",EDGE,{"disambiguationData":[OSD([subQ0]),TDD([makeQuery(id+"F0.imprint","IMPRINT",EDGE,{"disambiguationData":[TD([[makeQuery(id+"F0.imprint","INTERSECT",VERTEX,{"derivedFrom":[sQuery(id+"F0.wireOp",EDGE,"E0.1"),subQ0]}),-1.0]])],"derivedFrom":subQ0})])],"isStart":false});}
            var Q33;
            {var subQ0=sQuery(id+"F0.wireOp",EDGE,"E80");Q33=makeQuery(id+"F2.opExtrude","CAP_EDGE",EDGE,{"disambiguationData":[OSD([subQ0]),TDD([makeQuery(id+"F0.imprint","IMPRINT",EDGE,{"disambiguationData":[TD([[makeQuery(id+"F0.imprint","INTERSECT",VERTEX,{"derivedFrom":[sQuery(id+"F0.wireOp",EDGE,"E0.1"),subQ0]}),-1.0]])],"derivedFrom":subQ0})])],"isStart":false});}
            var Q34;
            {var subQ0=sQuery(id+"F0.wireOp",EDGE,"E80");Q34=makeQuery(id+"F2.opExtrude","CAP_EDGE",EDGE,{"disambiguationData":[OSD([subQ0]),TDD([makeQuery(id+"F0.imprint","IMPRINT",EDGE,{"disambiguationData":[TD([[makeQuery(id+"F0.imprint","INTERSECT",VERTEX,{"derivedFrom":[subQ0,sQuery(id+"F0.wireOp",EDGE,"E86.left")]}),-1.0]])],"derivedFrom":subQ0})])],"isStart":false});}
            var Q35;
            {var subQ0=sQuery(id+"F0.wireOp",EDGE,"E80");Q35=makeQuery(id+"F2.opExtrude","CAP_EDGE",EDGE,{"disambiguationData":[OSD([subQ0]),TDD([makeQuery(id+"F0.imprint","IMPRINT",EDGE,{"disambiguationData":[TD([[makeQuery(id+"F0.imprint","INTERSECT",VERTEX,{"derivedFrom":[sQuery(id+"F0.wireOp",EDGE,"E0.2"),subQ0]}),1.0]])],"derivedFrom":subQ0})])],"isStart":false});}
            var Q36;
            Q36=makeQuery(id+"F2.opExtrude","CAP_EDGE",EDGE,{"disambiguationData":[OSD([sQuery(id+"F0.wireOp",EDGE,"E86.left")])],"isStart":false});
            var Q37;
            Q37=makeQuery(id+"F2.opExtrude","CAP_EDGE",EDGE,{"disambiguationData":[OSD([sQuery(id+"F0.wireOp",EDGE,"E68")])],"isStart":false});
            var Q38;
            Q38=makeQuery(id+"F2.opExtrude","CAP_EDGE",EDGE,{"disambiguationData":[OSD([sQuery(id+"F0.wireOp",EDGE,"E86.right")])],"isStart":false});
            var Q39;
            Q39=makeQuery(id+"F2.opExtrude","CAP_EDGE",EDGE,{"disambiguationData":[OSD([sQuery(id+"F0.wireOp",EDGE,"E87.right")])],"isStart":false});
            var Q40;
            Q40=makeQuery(id+"F2.opExtrude","CAP_EDGE",EDGE,{"disambiguationData":[OSD([sQuery(id+"F0.wireOp",EDGE,"E87.left")])],"isStart":false});
            var Q41;
            {var subQ0=sQuery(id+"F0.wireOp",EDGE,"E81");Q41=makeQuery(id+"F2.opExtrude","CAP_EDGE",EDGE,{"disambiguationData":[OSD([subQ0]),TDD([makeQuery(id+"F0.imprint","IMPRINT",EDGE,{"disambiguationData":[TD([[makeQuery(id+"F0.imprint","INTERSECT",VERTEX,{"derivedFrom":[sQuery(id+"F0.wireOp",EDGE,"E0.2"),subQ0]}),1.0]])],"derivedFrom":subQ0})])],"isStart":false});}
            var Q42;
            Q42=makeQuery(id+"F2.opExtrude","CAP_EDGE",EDGE,{"disambiguationData":[OSD([sQuery(id+"F0.wireOp",EDGE,"E72"),sQuery(id+"F0.wireOp",EDGE,"E86.bottom")])],"isStart":false});
            var Q43;
            Q43=makeQuery(id+"F2.opExtrude","CAP_EDGE",EDGE,{"disambiguationData":[OSD([sQuery(id+"F0.wireOp",EDGE,"E77"),sQuery(id+"F0.wireOp",EDGE,"E87.bottom")])],"isStart":false});
            var Q44;
            Q44=makeQuery(id+"F2.opExtrude","CAP_EDGE",EDGE,{"disambiguationData":[OSD([sQuery(id+"F0.wireOp",EDGE,"E85.left")])],"isStart":false});
            var Q45;
            Q45=makeQuery(id+"F2.opExtrude","CAP_EDGE",EDGE,{"disambiguationData":[OSD([sQuery(id+"F0.wireOp",EDGE,"E85.right")])],"isStart":false});
            var Q46;
            Q46=makeQuery(id+"F2.opExtrude","CAP_EDGE",EDGE,{"disambiguationData":[OSD([sQuery(id+"F0.wireOp",EDGE,"E84.right")])],"isStart":false});
            var Q47;
            Q47=makeQuery(id+"F2.opExtrude","CAP_EDGE",EDGE,{"disambiguationData":[OSD([sQuery(id+"F0.wireOp",EDGE,"E84.left")])],"isStart":false});
            var Q48;
            Q48=makeQuery(id+"F2.opExtrude","CAP_EDGE",EDGE,{"disambiguationData":[OSD([sQuery(id+"F0.wireOp",EDGE,"E83.left")])],"isStart":false});
            var Q49;
            {var subQ0=sQuery(id+"F0.wireOp",EDGE,"E0.0");Q49=makeQuery(id+"F2.opExtrude","CAP_EDGE",EDGE,{"disambiguationData":[OSD([subQ0]),TDD([makeQuery(id+"F0.imprint","IMPRINT",EDGE,{"disambiguationData":[TD([[makeQuery(id+"F0.imprint","INTERSECT",VERTEX,{"derivedFrom":[subQ0,sQuery(id+"F0.wireOp",EDGE,"E0.1")]}),1.0]])],"derivedFrom":subQ0})])],"isStart":false});}
            var Q50;
            Q50=makeQuery(id+"F2.opExtrude","CAP_EDGE",EDGE,{"disambiguationData":[OSD([sQuery(id+"F0.wireOp",EDGE,"E83.right")])],"isStart":false});
            var Q51;
            {var subQ0=sQuery(id+"F0.wireOp",EDGE,"E0.0");Q51=makeQuery(id+"F2.opExtrude","CAP_EDGE",EDGE,{"disambiguationData":[OSD([subQ0]),TDD([makeQuery(id+"F0.imprint","IMPRINT",EDGE,{"disambiguationData":[TD([[makeQuery(id+"F0.imprint","INTERSECT",VERTEX,{"derivedFrom":[subQ0,sQuery(id+"F0.wireOp",EDGE,"E83.top"),sQuery(id+"F0.wireOp",EDGE,"E83.left")]}),1.0]])],"derivedFrom":subQ0})])],"isStart":false});}
            var Q52;
            {var subQ0=sQuery(id+"F0.wireOp",EDGE,"E0.0");Q52=makeQuery(id+"F2.opExtrude","CAP_EDGE",EDGE,{"disambiguationData":[OSD([subQ0]),TDD([makeQuery(id+"F0.imprint","IMPRINT",EDGE,{"disambiguationData":[TD([[makeQuery(id+"F0.imprint","INTERSECT",VERTEX,{"derivedFrom":[subQ0,sQuery(id+"F0.wireOp",EDGE,"E84.top"),sQuery(id+"F0.wireOp",EDGE,"E84.left")]}),1.0]])],"derivedFrom":subQ0})])],"isStart":false});}
            var Q53;
            {var subQ0=sQuery(id+"F0.wireOp",EDGE,"E0.0");Q53=makeQuery(id+"F2.opExtrude","CAP_EDGE",EDGE,{"disambiguationData":[OSD([subQ0]),TDD([makeQuery(id+"F0.imprint","IMPRINT",EDGE,{"disambiguationData":[TD([[makeQuery(id+"F0.imprint","INTERSECT",VERTEX,{"derivedFrom":[subQ0,sQuery(id+"F0.wireOp",EDGE,"E0.2")]}),-1.0]])],"derivedFrom":subQ0})])],"isStart":false});}
            var Q54;
            {var subQ0=sQuery(id+"F0.wireOp",EDGE,"E82");var subQ1=sQuery(id+"F0.wireOp",EDGE,"E0.1");var subQ2=sQuery(id+"F0.wireOp",EDGE,"E5");var subQ3=sQuery(id+"F0.wireOp",EDGE,"E1");Q54=makeQuery(id+"F2.boolean.opBoolean","SPLIT",EDGE,{"disambiguationData":[TD([makeQuery(id+"F2.opExtrude","SWEPT_FACE",FACE,{"disambiguationData":[OSD([subQ1]),TDD([makeQuery(id+"F0.imprint","IMPRINT",EDGE,{"disambiguationData":[TD([[makeQuery(id+"F0.imprint","INTERSECT",VERTEX,{"derivedFrom":[subQ1,subQ0]}),-1.0]])],"derivedFrom":subQ1})])]})])],"derivedFrom":makeQuery(id+"F1.opExtrude","CAP_EDGE",EDGE,{"disambiguationData":[OSD([subQ3,subQ2])],"isStart":false})});}
            var Q55;
            Q55=makeQuery(id+"F1.opExtrude","CAP_EDGE",EDGE,{"disambiguationData":[OSD([sQuery(id+"F0.wireOp",EDGE,"E7")])],"isStart":false});
            var Q56;
            Q56=makeQuery(id+"F1.opExtrude","CAP_EDGE",EDGE,{"disambiguationData":[OSD([sQuery(id+"F0.wireOp",EDGE,"E4")])],"isStart":false});
            var Q57;
            Q57=makeQuery(id+"F1.opExtrude","CAP_EDGE",EDGE,{"disambiguationData":[OSD([sQuery(id+"F0.wireOp",EDGE,"E8")])],"isStart":false});
            var Q58;
            Q58=makeQuery(id+"F1.opExtrude","CAP_EDGE",EDGE,{"disambiguationData":[OSD([sQuery(id+"F0.wireOp",EDGE,"E11")])],"isStart":false});
            var Q59;
            Q59=makeQuery(id+"F1.opExtrude","CAP_EDGE",EDGE,{"disambiguationData":[OSD([sQuery(id+"F0.wireOp",EDGE,"E10")])],"isStart":false});
            var Q60;
            Q60=makeQuery(id+"F1.opExtrude","CAP_EDGE",EDGE,{"disambiguationData":[OSD([sQuery(id+"F0.wireOp",EDGE,"E2")])],"isStart":false});
            var Q61;
            {var subQ1=sQuery(id+"F0.wireOp",EDGE,"E5");var subQ2=sQuery(id+"F0.wireOp",EDGE,"E1");var subQ3=sQuery(id+"F0.wireOp",EDGE,"E2");Q61=makeQuery(id+"F2.boolean.opBoolean","SPLIT",EDGE,{"disambiguationData":[TD([makeQuery(id+"F1.opExtrude","SWEPT_FACE",FACE,{"disambiguationData":[OSD([subQ3])]})])],"derivedFrom":makeQuery(id+"F1.opExtrude","CAP_EDGE",EDGE,{"disambiguationData":[OSD([subQ2,subQ1])],"isStart":false})});}
            var Q62;
            Q62=makeQuery(id+"F1.opExtrude","CAP_EDGE",EDGE,{"disambiguationData":[OSD([sQuery(id+"F0.wireOp",EDGE,"E12")])],"isStart":false});
            var Q63;
            {var subQ1=sQuery(id+"F0.wireOp",EDGE,"E5");var subQ2=sQuery(id+"F0.wireOp",EDGE,"E1");var subQ3=sQuery(id+"F0.wireOp",EDGE,"E4");Q63=makeQuery(id+"F2.boolean.opBoolean","SPLIT",EDGE,{"disambiguationData":[TD([makeQuery(id+"F1.opExtrude","SWEPT_FACE",FACE,{"disambiguationData":[OSD([subQ3])]})])],"derivedFrom":makeQuery(id+"F1.opExtrude","CAP_EDGE",EDGE,{"disambiguationData":[OSD([subQ2,subQ1])],"isStart":false})});}
            fillet(context, id + "F5", {"entities" : qUnion([Q0, Q1, Q2, Q3, Q4, Q5, Q6, Q7, Q8, Q9, Q10, Q11, Q12, Q13, Q14, Q15, Q16, Q17, Q18, Q19, Q20, Q21, Q22, Q23, Q24, Q25, Q26, Q27, Q28, Q29, Q30, Q31, Q32, Q33, Q34, Q35, Q36, Q37, Q38, Q39, Q40, Q41, Q42, Q43, Q44, Q45, Q46, Q47, Q48, Q49, Q50, Q51, Q52, Q53, Q54, Q55, Q56, Q57, Q58, Q59, Q60, Q61, Q62, Q63]), "radius" : 0.5 * mm, "tangentPropagation" : true, "allowEdgeOverflow" : false});
        }
    });
